FREECAD ASSEMBLY — COMPONENT RECIPES ("feeder_assembly")

This assembly document has 52 components, labeled P0..P51 below (a component is one placed body or linked part). 40 of them carry a construction recipe — the FreeCAD feature program that regenerates the part from scratch, quoted from this document or its linked companion documents; the rest are supplied as boundary geometry only. No exploded tour is included for this assembly.
NOTE — document 2 of 3 of this assembly tour. The two overview renders and the header above are repeated from document 1; the component sections below continue where the previous document stopped.
COMPONENT P15 — recipe-attached ("Body-slide_mid_v3", modeled in this document).
Construction recipe (the document's own serialized feature program — sketch geometry with constraints, then the solid features built on it; lengths are millimeters unless a unit is written):

FEATURE [Sketcher::SketchObject] Sketch077
  FullyConstrained = true
  MapMode = 5
  Support = -> [XY_Plane016]
  sketch-geometry (6):
    g0: LineSegment StartX=-11 StartY=0 StartZ=0 EndX=11 EndY=0 EndZ=0
    g1: LineSegment StartX=11 StartY=0 StartZ=0 EndX=11 EndY=-214 EndZ=0
    g2: LineSegment StartX=11 StartY=-214 StartZ=0 EndX=-11 EndY=-214 EndZ=0
    g3: LineSegment StartX=-11 StartY=-214 StartZ=0 EndX=-11 EndY=0 EndZ=0
    g4: LineSegment StartX=-11 StartY=0 StartZ=0 EndX=0 EndY=0 EndZ=0
    g5: LineSegment StartX=0 StartY=0 StartZ=0 EndX=11 EndY=0 EndZ=0
  constraints (16):
    c: Coincident(g0,g1)
    c: Coincident(g1,g2)
    c: Coincident(g2,g3)
    c: Horizontal(g0)
    c: Horizontal(g2)
    c: Vertical(g1)
    c: Vertical(g3)
    c: DistanceX(g0,g0) = 22
    c: DistanceY(g3,g3) = 214
    c: Coincident(g0,g3)
    c: PointOnObject(g-1,g0)
    c: Coincident(g4,g0)
    c: Coincident(g4,g-1)
    c: Coincident(g5,g4)
    c: Coincident(g5,g0)
    c: Equal(g4,g5)
FEATURE [PartDesign::Pad] Pad030  label="Pad-base_plate"
  Direction = (0,0,1)
  Length = 8
  Length2 = 10
  Profile = -> Sketch077
  ReferenceAxis = -> Sketch077 [N_Axis]
  Type = 0
FEATURE [Sketcher::SketchObject] Sketch078
  FullyConstrained = true
  MapMode = 5
  Placement = pos=(-11,0,0) rot=(0.57735,-0.57735,-0.57735;2.0944rad)
  Support = -> [Pad030]
FEATURE [Sketcher::SketchObject] Sketch079
  ExternalGeometry = -> [Pad030]
  FullyConstrained = true
  MapMode = 5
  Placement = pos=(0,0,8) rot=(0,0,1;0rad)
  Support = -> [Pad030]
  sketch-geometry (4):
    g0: LineSegment StartX=-11 StartY=2.5 StartZ=0 EndX=11 EndY=2.5 EndZ=0
    g1: LineSegment StartX=11 StartY=2.5 StartZ=0 EndX=11 EndY=-22.5 EndZ=0
    g2: LineSegment StartX=11 StartY=-22.5 StartZ=0 EndX=-11 EndY=-22.5 EndZ=0
    g3: LineSegment StartX=-11 StartY=-22.5 StartZ=0 EndX=-11 EndY=2.5 EndZ=0
  constraints (12):
    c: Coincident(g0,g1)
    c: Coincident(g1,g2)
    c: Coincident(g2,g3)
    c: Horizontal(g0)
    c: Horizontal(g2)
    c: Vertical(g1)
    c: Vertical(g3)
    c: DistanceY(g1,g1) = 25
    c: Coincident(g3,g0)
    c: PointOnObject(g1,g-3)
    c: Vertical(g0,g-4)
    c: DistanceY(g-4,g0) = 2.5
FEATURE [PartDesign::Pad] Pad031  label="Pad-bearing_mount_base"
  BaseFeature = -> Pad030
  Direction = (0,0,1)
  Length = 20
  Length2 = 8
  Profile = -> Sketch079
  ReferenceAxis = -> Sketch079 [N_Axis]
  Type = 4
FEATURE [Sketcher::SketchObject] Sketch080
  FullyConstrained = true
  MapMode = 5
  Placement = pos=(-11,0,0) rot=(0.57735,-0.57735,-0.57735;2.0944rad)
  Support = -> [Pad031]
  sketch-geometry (1):
    g0: Circle CenterX=10 CenterY=15 CenterZ=0 NormalX=0 NormalY=0 NormalZ=1 AngleXU=0 Radius=11.01
  constraints (3):
    c: DistanceX(g0) = 10
    c: DistanceY(g0) = 15
    c: Diameter(g0) = 22.02
FEATURE [PartDesign::Pocket] Pocket039  label="Pocket-bearing-OD"
  BaseFeature = -> Pad031
  Direction = (1,0,0)
  Length = 7
  Length2 = 5
  Profile = -> Sketch080
  ReferenceAxis = -> Sketch080 [N_Axis]
  Type = 0
FEATURE [PartDesign::Mirrored] Mirrored001  label="Mirrored-bearing_pocket"
  BaseFeature = -> Pocket039
  MirrorPlane = -> YZ_Plane016
  Originals = -> [Pocket039]
FEATURE [Sketcher::SketchObject] Sketch081
  ExternalGeometry = -> [Mirrored001]
  FullyConstrained = true
  MapMode = 5
  Placement = pos=(-4,0,0) rot=(0.57735,-0.57735,-0.57735;2.0944rad)
  Support = -> [Mirrored001]
  sketch-geometry (1):
    g0: Circle CenterX=10 CenterY=15 CenterZ=0 NormalX=0 NormalY=0 NormalZ=1 AngleXU=0 Radius=10
  constraints (2):
    c: Coincident(g0,g-3)
    c: Diameter(g0) = 20
FEATURE [PartDesign::Pocket] Pocket040
  BaseFeature = -> Mirrored001
  Direction = (1,0,0)
  Length = 5
  Length2 = 5
  Profile = -> Sketch081
  ReferenceAxis = -> Sketch081 [N_Axis]
  Type = 1
FEATURE [Sketcher::SketchObject] Sketch083
  ExternalGeometry = -> [Pocket040]
  FullyConstrained = false
  MapMode = 5
  Placement = pos=(-11,0,0) rot=(0.57735,-0.57735,-0.57735;2.0944rad)
  Support = -> [Pocket040]
  sketch-geometry (31):
    g0: LineSegment StartX=17.5 StartY=28 StartZ=0 EndX=17.5 EndY=93.7475 EndZ=0
    g1: LineSegment StartX=17.5 StartY=93.7475 StartZ=0 EndX=202.5 EndY=26.413 EndZ=0
    g2: LineSegment StartX=202.5 StartY=26.413 StartZ=0 EndX=202.5 EndY=8 EndZ=0
    g3: LineSegment StartX=165.375 StartY=8 StartZ=0 EndX=112 EndY=27.427 EndZ=0
    g4: LineSegment StartX=25 StartY=59.0924 StartZ=0 EndX=25 EndY=8 EndZ=0
    g5: LineSegment StartX=25 StartY=8 StartZ=0 EndX=22.5 EndY=8 EndZ=0
    g6: LineSegment StartX=22.5 StartY=8 StartZ=0 EndX=22.5 EndY=28 EndZ=0
    g7: LineSegment StartX=22.5 StartY=28 StartZ=0 EndX=17.5 EndY=28 EndZ=0
    g8: ArcOfCircle CenterX=30.2523 CenterY=73.1434 CenterZ=0 NormalX=0 NormalY=0 NormalZ=1 AngleXU=0 Radius=8 StartAngle=1.22173 EndAngle=4.36332
    g9: LineSegment StartX=27.5161 StartY=65.6259 StartZ=0 EndX=187.264 EndY=7.48246 EndZ=0
    g10: LineSegment StartX=192.736 StartY=22.5175 StartZ=0 EndX=32.9884 EndY=80.661 EndZ=0
    g11: LineSegment StartX=30.2523 StartY=73.1434 StartZ=0 EndX=190 EndY=15 EndZ=0
    g12: LineSegment StartX=77.1149 StartY=56.0868 StartZ=0 EndX=71.9846 EndY=41.9914 EndZ=0
    g13: LineSegment StartX=82.2452 StartY=70.1822 StartZ=0 EndX=77.1149 EndY=56.0868 EndZ=0
    g14: LineSegment StartX=102 StartY=31.0667 StartZ=0 EndX=102 EndY=8 EndZ=0
    g15: LineSegment StartX=102 StartY=8 StartZ=0 EndX=112 EndY=8 EndZ=0
    g16: LineSegment StartX=112 StartY=8 StartZ=0 EndX=112 EndY=27.427 EndZ=0
    g17: LineSegment StartX=102 StartY=31.0667 StartZ=0 EndX=25 EndY=59.0924 EndZ=0
    g18: GeomPoint X=72.1528 Y=42.4533 Z=0
    g19: LineSegment StartX=102 StartY=38.516 StartZ=0 EndX=102 EndY=55.5428 EndZ=0
    g20: LineSegment StartX=112 StartY=51.9031 StartZ=0 EndX=112 EndY=34.8763 EndZ=0
    g21: LineSegment StartX=32.9884 StartY=80.661 StartZ=0 EndX=102 EndY=55.5428 EndZ=0
    g22: LineSegment StartX=102 StartY=38.516 StartZ=0 EndX=27.5161 EndY=65.6259 EndZ=0
    g23: LineSegment StartX=112 StartY=51.9031 StartZ=0 EndX=192.736 EndY=22.5175 EndZ=0
    g24: LineSegment StartX=185.842 StartY=8 StartZ=0 EndX=165.375 EndY=8 EndZ=0
    g25: LineSegment StartX=202.5 StartY=8 StartZ=0 EndX=193.873 EndY=8 EndZ=0
    g26: LineSegment StartX=193.873 StartY=8 StartZ=0 EndX=185.842 EndY=8 EndZ=0
    g27: LineSegment StartX=187.264 StartY=7.48246 StartZ=0 EndX=185.842 EndY=8 EndZ=0
    g28: LineSegment StartX=185.842 StartY=8 StartZ=0 EndX=112 EndY=34.8763 EndZ=0
    g29: ArcOfCircle CenterX=190 CenterY=15 CenterZ=0 NormalX=0 NormalY=0 NormalZ=1 AngleXU=0 Radius=8 StartAngle=4.36332 EndAngle=5.21775
    g30: ArcOfCircle CenterX=190 CenterY=15 CenterZ=0 NormalX=0 NormalY=0 NormalZ=1 AngleXU=0 Radius=8 StartAngle=5.21775 EndAngle=7.50492
  constraints (84):
    c: PointOnObject(g0,g-5)
    c: Vertical(g0)
    c: Coincident(g1,g0)
    c: Coincident(g2,g1)
    c: PointOnObject(g2,g-3)
    c: Vertical(g2)
    c: PointOnObject(g25,g2)
    c: PointOnObject(g24,g-3)
    c: Coincident(g3,g24)
    c: Coincident(g4,g17)
    c: PointOnObject(g4,g-3)
    c: Vertical(g4)
    c: Coincident(g5,g4)
    c: Coincident(g5,g-4)
    c: Coincident(g6,g5)
    c: Coincident(g6,g-5)
    c: Coincident(g7,g6)
    c: Coincident(g7,g0)
    c: Parallel(g3,g1)
    c: Tangent(g8,g9) = -1.5708
    c: Tangent(g9,g29) = -1.5708
    c: Tangent(g30,g10) = -1.5708
    c: Tangent(g10,g8) = -1.5708
    c: Diameter(g8) = 16
    c: Coincident(g11,g8)
    c: Coincident(g11,g29)
    c: Parallel(g11,g3)
    c: Angle(g3,g-3) = 0.349066
    c: PointOnObject(g12,g11)
    c: PointOnObject(g12,g3)
    c: Angle(g3,g12) = 1.5708
    c: PointOnObject(g13,g1)
    c: Coincident(g13,g12)
    c: Parallel(g13,g12)
    c: Distance(g12,g17) = 50
    c: Distance(g13) = 15
    c: Distance(g12) = 15
    c: Distance(g10) = 170
    c: DistanceY(g2,g29) = 7
    c: DistanceX(g-5,g0) = 20
    c: DistanceX(g0,g4) = 7.5
    c: DistanceX(g4,g2) = 177.5
    c: DistanceX(g29,g2) = 12.5
    c: PointOnObject(g14,g-3)
    c: Coincident(g15,g14)
    c: PointOnObject(g15,g-3)
    c: Coincident(g16,g15)
    c: Vertical(g16)
    c: Vertical(g14)
    c: DistanceX(g15,g15) = 10
    c: DistanceX(g0,g14) = 84.5
    c: Coincident(g3,g16)
    c: Coincident(g17,g14)
    c: Parallel(g17,g3)
    c: PointOnObject(g18,g12)
    c: PointOnObject(g12,g17)
    c: PointOnObject(g19,g9)
    c: PointOnObject(g19,g10)
    c: PointOnObject(g20,g10)
    c: PointOnObject(g20,g9)
    c: Vertical(g20)
    c: Vertical(g14,g19)
    c: Vertical(g20,g3)
    c: Vertical(g19)
    c: Coincident(g21,g8)
    c: Coincident(g21,g19)
    c: Coincident(g22,g19)
    c: Coincident(g22,g8)
    c: Coincident(g23,g20)
    c: Coincident(g23,g30)
    c: Coincident(g27,g29)
    c: Coincident(g20,g28)
    c: Coincident(g26,g24)
    c: Horizontal(g24)
    c: Coincident(g25,g26)
    c: Horizontal(g25)
    c: Horizontal(g26)
    c: Coincident(g27,g28)
    c: Coincident(g27,g24)
    c: PointOnObject(g24,g9)
    c: Coincident(g29,g30)
    c: Coincident(g29,g30)
    c: Equal(g8,g29)
    c: Coincident(g25,g29)
FEATURE [PartDesign::Pad] Pad033  label="Pad-ramp001"
  BaseFeature = -> Pocket040
  Direction = (-1,0,0)
  Length = 22
  Length2 = 10
  Profile = -> Sketch083
  ReferenceAxis = -> Sketch083 [N_Axis]
  Reversed = true
  Type = 0
FEATURE [Sketcher::SketchObject] Sketch085
  ExternalGeometry = -> [Pad033]
  FullyConstrained = true
  MapMode = 5
  Placement = pos=(-11,0,0) rot=(0.57735,-0.57735,-0.57735;2.0944rad)
  Support = -> [Pad033]
  sketch-geometry (6):
    g0: ArcOfCircle CenterX=30.2523 CenterY=73.1434 CenterZ=0 NormalX=0 NormalY=0 NormalZ=1 AngleXU=0 Radius=11.25 StartAngle=1.22173 EndAngle=4.36332
    g1: ArcOfCircle CenterX=190 CenterY=15 CenterZ=0 NormalX=0 NormalY=0 NormalZ=1 AngleXU=0 Radius=11.25 StartAngle=4.36332 EndAngle=7.50492
    g2: LineSegment StartX=26.4045 StartY=62.5719 StartZ=0 EndX=186.152 EndY=4.42846 EndZ=0
    g3: LineSegment StartX=193.848 StartY=25.5715 StartZ=0 EndX=34.1 EndY=83.715 EndZ=0
    g4: LineSegment StartX=30.2523 StartY=73.1434 StartZ=0 EndX=190 EndY=15 EndZ=0
    g5: LineSegment StartX=55.3826 StartY=79.9594 StartZ=0 EndX=50.2523 EndY=65.864 EndZ=0
  constraints (17):
    c: Tangent(g0,g2) = -1.5708
    c: Tangent(g2,g1) = -1.5708
    c: Tangent(g3,g0) = -1.5708
    c: Equal(g0,g1)
    c: Diameter(g0) = 22.5
    c: Coincident(g4,g0)
    c: Coincident(g4,g1)
    c: Distance(g3) = 170
    c: DistanceX(g1,g-3) = 12.5
    c: PointOnObject(g5,g-4)
    c: PointOnObject(g5,g4)
    c: Angle(g4,g5) = 1.5708
    c: Distance(g5) = 15
    c: Parallel(g-4,g4)
    c: Angle(g1) = 3.14159
    c: Coincident(g3,g1)
    c: DistanceX(g0,g5) = 20
FEATURE [PartDesign::Pocket] Pocket043  label="Pocket-bearing_slot001"
  BaseFeature = -> Pad033
  Direction = (1,0,0)
  Length = 7.5
  Length2 = 5
  Profile = -> Sketch085
  ReferenceAxis = -> Sketch085 [N_Axis]
  Type = 0
FEATURE [PartDesign::Mirrored] Mirrored003  label="Mirrored-bearing_slot"
  BaseFeature = -> Pocket043
  MirrorPlane = -> YZ_Plane016
  Originals = -> [Pocket043]
FEATURE [Sketcher::SketchObject] Sketch094
  ExternalGeometry = -> [Mirrored003]
  FullyConstrained = true
  MapMode = 5
  Placement = pos=(-3.5,0,0) rot=(0.57735,-0.57735,-0.57735;2.0944rad)
  Support = -> [Mirrored003]
  sketch-geometry (4):
    g0: LineSegment StartX=112 StartY=34.8763 StartZ=0 EndX=102 EndY=38.516 EndZ=0
    g1: LineSegment StartX=102 StartY=38.516 StartZ=0 EndX=102 EndY=55.5428 EndZ=0
    g2: LineSegment StartX=102 StartY=55.5428 StartZ=0 EndX=112 EndY=51.9031 EndZ=0
    g3: LineSegment StartX=112 StartY=51.9031 StartZ=0 EndX=112 EndY=34.8763 EndZ=0
  constraints (8):
    c: Coincident(g1,g0)
    c: Coincident(g2,g1)
    c: Coincident(g3,g2)
    c: Coincident(g3,g0)
    c: Coincident(g1,g-4)
    c: Coincident(g0,g-4)
    c: Coincident(g-3,g2)
    c: Coincident(g-3,g0)
FEATURE [PartDesign::Pocket] Pocket044  label="Pocket-mid_support_inside"
  BaseFeature = -> Mirrored003
  Direction = (1,0,0)
  Length = 2.5
  Length2 = 5
  Profile = -> Sketch094
  ReferenceAxis = -> Sketch094 [N_Axis]
  Type = 0
FEATURE [PartDesign::Mirrored] Mirrored004
  BaseFeature = -> Pocket044
  MirrorPlane = -> YZ_Plane016
  Originals = -> [Pocket044]
FEATURE [Sketcher::SketchObject] Sketch095
  ExternalGeometry = -> [Mirrored004,Sketch085]
  FullyConstrained = true
  MapMode = 5
  Placement = pos=(-11,0,0) rot=(0.57735,-0.57735,-0.57735;2.0944rad)
  Support = -> [Mirrored004]
  sketch-geometry (9):
    g0: LineSegment StartX=17.5 StartY=93.7475 StartZ=0 EndX=202.5 EndY=26.413 EndZ=0
    g1: LineSegment StartX=202.5 StartY=26.413 StartZ=0 EndX=202.5 EndY=0 EndZ=0
    g2: LineSegment StartX=202.5 StartY=0 StartZ=0 EndX=187.355 EndY=0 EndZ=0
    g3: LineSegment StartX=187.355 StartY=0 StartZ=0 EndX=17.5 EndY=61.8222 EndZ=0
    g4: LineSegment StartX=17.5 StartY=61.8222 StartZ=0 EndX=17.5 EndY=93.7475 EndZ=0
    g5: ArcOfCircle CenterX=30.2523 CenterY=73.1434 CenterZ=0 NormalX=0 NormalY=0 NormalZ=1 AngleXU=0 Radius=6 StartAngle=1.22173 EndAngle=4.36332
    g6: ArcOfCircle CenterX=190 CenterY=15 CenterZ=0 NormalX=0 NormalY=0 NormalZ=1 AngleXU=0 Radius=6 StartAngle=4.36332 EndAngle=7.50492
    g7: LineSegment StartX=28.2001 StartY=67.5053 StartZ=0 EndX=187.948 EndY=9.36184 EndZ=0
    g8: LineSegment StartX=192.052 StartY=20.6382 StartZ=0 EndX=32.3044 EndY=78.7816 EndZ=0
  constraints (21):
    c: Coincident(g0,g-4)
    c: Coincident(g0,g-6)
    c: Coincident(g1,g0)
    c: PointOnObject(g1,g-7)
    c: Vertical(g1)
    c: Coincident(g2,g1)
    c: PointOnObject(g2,g-7)
    c: Coincident(g3,g2)
    c: PointOnObject(g3,g-4)
    c: Coincident(g4,g3)
    c: Coincident(g4,g0)
    c: Parallel(g-5,g3)
    c: PointOnObject(g-5,g3)
    c: Tangent(g5,g7) = -1.5708
    c: Tangent(g7,g6) = -1.5708
    c: Tangent(g6,g8) = -1.5708
    c: Tangent(g8,g5) = -1.5708
    c: Equal(g5,g6)
    c: Coincident(g5,g-9)
    c: Coincident(g6,g-8)
    c: Diameter(g6) = 12
FEATURE [PartDesign::Pad] Pad039  label="Pad-bearing_cap"
  BaseFeature = -> Mirrored004
  Direction = (-1,0,0)
  Length = 2.5
  Length2 = 10
  Profile = -> Sketch095
  ReferenceAxis = -> Sketch095 [N_Axis]
  Type = 0
FEATURE [PartDesign::Mirrored] Mirrored005
  BaseFeature = -> Pad039
  MirrorPlane = -> YZ_Plane016
  Originals = -> [Pad039]
FEATURE [PartDesign::Fillet] Fillet021
  Base = -> Mirrored005 [Edge81,Edge94,Edge122]
  BaseFeature = -> Mirrored005
  Radius = 14
  SupportTransform = false
  UseAllEdges = false
FEATURE [PartDesign::Fillet] Fillet022
  Base = -> Fillet021 [Edge45]
  BaseFeature = -> Fillet021
  Radius = 14
  SupportTransform = false
  UseAllEdges = false
FEATURE [PartDesign::Fillet] Fillet023  label="Fillet-bottom_face_to_vertical"
  Base = -> Fillet022 [Edge121,Edge122,Edge120]
  BaseFeature = -> Fillet022
  Radius = 2
  SupportTransform = false
  UseAllEdges = false
FEATURE [PartDesign::Fillet] Fillet024  label="Fillet-acute_end_angle"
  Base = -> Fillet023 [Edge32]
  BaseFeature = -> Fillet023
  Radius = 2
  SupportTransform = false
  UseAllEdges = false
FEATURE [PartDesign::Fillet] Fillet025
  Base = -> Fillet024 [Edge107]
  BaseFeature = -> Fillet024
  Radius = 5
  SupportTransform = false
  UseAllEdges = false
FEATURE [PartDesign::Fillet] Fillet026
  Base = -> Fillet025 [Edge62]
  BaseFeature = -> Fillet025
  Radius = 12
  SupportTransform = false
  UseAllEdges = false
FEATURE [PartDesign::Fillet] Fillet027
  Base = -> Fillet026 [Edge25]
  BaseFeature = -> Fillet026
  Radius = 2
  SupportTransform = false
  UseAllEdges = false
FEATURE [PartDesign::Fillet] Fillet028
  Base = -> Fillet027 [Edge231,Edge246]
  BaseFeature = -> Fillet027
  Radius = 3
  SupportTransform = false
  UseAllEdges = false
FEATURE [PartDesign::Fillet] Fillet029
  Base = -> Fillet028 [Edge51,Edge54]
  BaseFeature = -> Fillet028
  Radius = 3
  SupportTransform = false
  UseAllEdges = false
FEATURE [PartDesign::Fillet] Fillet030  label="Fillet-extender_main_curvature"
  Base = -> Fillet029 [Edge176,Edge209]
  BaseFeature = -> Fillet029
  Radius = 10
  SupportTransform = false
  UseAllEdges = false
FEATURE [PartDesign::Fillet] Fillet031  label="Fillet-bearing_face"
  Base = -> Fillet030 [Face16]
  BaseFeature = -> Fillet030
  Radius = 0.4
  SupportTransform = false
  UseAllEdges = false
FEATURE [PartDesign::Fillet] Fillet032  label="Fillet-bearing_face_mirror"
  Base = -> Fillet031 [Face28]
  BaseFeature = -> Fillet031
  Radius = 0.4
  SupportTransform = false
  UseAllEdges = false
FEATURE [PartDesign::Fillet] Fillet033
  Base = -> Fillet032 [Face96,Face112]
  BaseFeature = -> Fillet032
  Radius = 1
  SupportTransform = false
  UseAllEdges = false
FEATURE [PartDesign::Fillet] Fillet034
  Base = -> Fillet033 [Face119,Face4]
  BaseFeature = -> Fillet033
  Radius = 0.4
  SupportTransform = false
  UseAllEdges = false
FEATURE [Sketcher::SketchObject] Sketch098
  ExternalGeometry = -> [Fillet021]
  FullyConstrained = true
  MapMode = 5
  Placement = pos=(0,0,8) rot=(0,0,1;0rad)
  Support = -> [Fillet034]
  sketch-geometry (8):
    g0: ArcOfCircle CenterX=-2e-16 CenterY=-40 CenterZ=0 NormalX=0 NormalY=0 NormalZ=1 AngleXU=0 Radius=6 StartAngle=-1.8e-15 EndAngle=3.14159
    g1: ArcOfCircle CenterX=0 CenterY=-80 CenterZ=0 NormalX=0 NormalY=0 NormalZ=1 AngleXU=0 Radius=6 StartAngle=3.14159 EndAngle=6.28319
    g2: LineSegment StartX=-6 StartY=-40 StartZ=0 EndX=-6 EndY=-80 EndZ=0
    g3: LineSegment StartX=6 StartY=-80 StartZ=0 EndX=6 EndY=-40 EndZ=0
    g4: ArcOfCircle CenterX=0 CenterY=-120 CenterZ=0 NormalX=0 NormalY=0 NormalZ=1 AngleXU=0 Radius=6 StartAngle=4e-16 EndAngle=3.14159
    g5: ArcOfCircle CenterX=0 CenterY=-140 CenterZ=0 NormalX=0 NormalY=0 NormalZ=1 AngleXU=0 Radius=6 StartAngle=3.14159 EndAngle=6.28319
    g6: LineSegment StartX=-6 StartY=-120 StartZ=0 EndX=-6 EndY=-140 EndZ=0
    g7: LineSegment StartX=6 StartY=-140 StartZ=0 EndX=6 EndY=-120 EndZ=0
  constraints (20):
    c: Tangent(g0,g2) = -1.5708
    c: Tangent(g2,g1) = -1.5708
    c: Tangent(g1,g3) = -1.5708
    c: Tangent(g3,g0) = -1.5708
    c: Equal(g0,g1)
    c: DistanceX(g-3,g0) = 11
    c: Diameter(g1) = 12
    c: DistanceY(g0) = -40
    c: DistanceY(g2,g2) = 40
    c: Tangent(g4,g6) = -1.5708
    c: Tangent(g6,g5) = -1.5708
    c: Tangent(g5,g7) = -1.5708
    c: Tangent(g7,g4) = -1.5708
    c: Equal(g4,g5)
    c: PointOnObject(g4,g-2)
    c: PointOnObject(g5,g-2)
    c: DistanceY(g6,g6) = 20
    c: Diameter(g5) = 12
    c: DistanceY(g4,g1) = 40
    c: PointOnObject(g1,g-2)
FEATURE [PartDesign::Pocket] Pocket051
  BaseFeature = -> Fillet034
  Direction = (0,0,-1)
  Length = 5
  Length2 = 5
  Profile = -> Sketch098
  ReferenceAxis = -> Sketch098 [N_Axis]
  Type = 0
FEATURE [Sketcher::SketchObject] Sketch100
  FullyConstrained = false
  MapMode = 5
  Placement = pos=(0,0,8) rot=(0,0,1;0rad)
  Support = -> [Pocket051]
  sketch-geometry (1):
    g0: Circle CenterX=0 CenterY=-207 CenterZ=0 NormalX=0 NormalY=0 NormalZ=1 AngleXU=0 Radius=6
  constraints (2):
    c: PointOnObject(g0,g-2)
    c: Diameter(g0) = 12
FEATURE [PartDesign::Pocket] Pocket052  label="Pocket-extender_inset"
  BaseFeature = -> Pocket051
  Direction = (0,0,-1)
  Length = 5
  Length2 = 40
  Profile = -> Sketch100
  ReferenceAxis = -> Sketch100 [N_Axis]
  Type = 4
FEATURE [Sketcher::SketchObject] Sketch101
  FullyConstrained = false
  MapMode = 5
  Placement = pos=(-11,0,0) rot=(0.57735,-0.57735,-0.57735;2.0944rad)
  sketch-geometry (9):
    g0: LineSegment StartX=25 StartY=59.0924 StartZ=0 EndX=25 EndY=55.5221 EndZ=0
    g1: LineSegment StartX=25 StartY=59.0924 StartZ=0 EndX=28.3551 EndY=57.8713 EndZ=0
    g2: ArcOfCircle CenterX=27.5 CenterY=55.5221 CenterZ=0 NormalX=0 NormalY=0 NormalZ=1 AngleXU=0 Radius=2.5 StartAngle=1.22173 EndAngle=3.14159
    g3: ArcOfCircle CenterX=97 CenterY=27.5657 CenterZ=0 NormalX=0 NormalY=0 NormalZ=1 AngleXU=0 Radius=5 StartAngle=2.0166e-12 EndAngle=1.22173
    g4: ArcOfCircle CenterX=114.5 CenterY=23.8566 CenterZ=0 NormalX=0 NormalY=0 NormalZ=1 AngleXU=0 Radius=2.5 StartAngle=1.22173 EndAngle=3.14159
    g5: LineSegment StartX=98.7101 StartY=32.2641 StartZ=0 EndX=102 EndY=31.0667 EndZ=0
    g6: LineSegment StartX=102 StartY=31.0667 StartZ=0 EndX=102 EndY=27.5657 EndZ=0
    g7: LineSegment StartX=112 StartY=23.8566 StartZ=0 EndX=112 EndY=27.427 EndZ=0
    g8: LineSegment StartX=112 StartY=27.427 StartZ=0 EndX=115.355 EndY=26.2059 EndZ=0
  constraints (18):
    c: Coincident(g1,g0)
    c: Coincident(g0,g2)
    c: Coincident(g1,g2)
    c: Diameter(g2) = 5
    c: Coincident(g5,g3)
    c: Coincident(g6,g5)
    c: Coincident(g6,g3)
    c: Coincident(g7,g4)
    c: Coincident(g8,g7)
    c: Coincident(g8,g4)
    c: Diameter(g3) = 10
    c: Angle(g3) = 1.22173
    c: Equal(g6,g5)
    c: Equal(g8,g7)
    c: Angle(g4) = 1.91986
    c: Equal(g0,g1)
    c: Angle(g2) = 1.91986
    c: Equal(g4,g2)
FEATURE [PartDesign::Body] Body017  label="Body-slide_mid_v3"
  Group = -> [Sketch077,Pad030,Sketch078,Sketch079,Pad031,Sketch080,Pocket039,Mirrored001,Sketch081,Pocket040,Sketch083,Pad033,Sketch085,Pocket043,Mirrored003,Sketch094,Pocket044,Mirrored004,Sketch095,Pad039,Mirrored005,Fillet021,Sketch098,Sketch100,Fillet022,Fillet023,Fillet024,Fillet025,Fillet026,Fillet027,Fillet028,Fillet029,Fillet030,Fillet031,Fillet032,Fillet033,Fillet034,Pocket051,Pocket052,Sketch101,+13 more]
  Origin = -> Origin016
  Tip = -> Fillet125
COMPONENT P16 — recipe-attached ("Body-bearing001", modeled in this document).
Construction recipe (the document's own serialized feature program — sketch geometry with constraints, then the solid features built on it; lengths are millimeters unless a unit is written):

FEATURE [Sketcher::SketchObject] Sketch082
  FullyConstrained = true
  MapMode = 5
  Support = -> [XY_Plane017]
  sketch-geometry (2):
    g0: Circle CenterX=0 CenterY=0 CenterZ=0 NormalX=0 NormalY=0 NormalZ=1 AngleXU=0 Radius=3.95
    g1: Circle CenterX=0 CenterY=0 CenterZ=0 NormalX=0 NormalY=0 NormalZ=1 AngleXU=0 Radius=11
  constraints (4):
    c: Coincident(g0,g-1)
    c: Coincident(g1,g0)
    c: Diameter(g0) = 7.9
    c: Diameter(g1) = 22
FEATURE [PartDesign::Pad] Pad032
  Direction = (0,0,1)
  Length = 7
  Length2 = 10
  Profile = -> Sketch082
  ReferenceAxis = -> Sketch082 [N_Axis]
  Type = 0
FEATURE [PartDesign::Body] Body018  label="Body-bearing001"
  Group = -> [Sketch082,Pad032]
  Origin = -> Origin017
  Placement = pos=(-3.26003,-10.1498,15.02) rot=(0,-1,0;1.5708rad)
  Tip = -> Pad032
COMPONENT P17 — recipe-attached ("Body-v3.1_slicer", modeled in this document).
Construction recipe (the document's own serialized feature program — sketch geometry with constraints, then the solid features built on it; lengths are millimeters unless a unit is written):

FEATURE [Sketcher::SketchObject] Sketch086
  FullyConstrained = true
  MapMode = 5
  Placement = pos=(0,0,0) rot=(1,0,0;1.5708rad)
  Support = -> [XZ_Plane018]
  sketch-geometry (16):
    g0: LineSegment StartX=-3.8476e-12 StartY=-10.8333 StartZ=0 EndX=4 EndY=-10.8333 EndZ=0
    g1: LineSegment StartX=4 StartY=-10.8333 StartZ=0 EndX=4 EndY=-0.833334 EndZ=0
    g2: LineSegment StartX=4 StartY=-0.833334 StartZ=0 EndX=-15 EndY=-0.833334 EndZ=0
    g3: LineSegment StartX=-15 StartY=-0.833334 StartZ=0 EndX=-15 EndY=0.833334 EndZ=0
    g4: LineSegment StartX=-15 StartY=0.833334 StartZ=0 EndX=4 EndY=0.833334 EndZ=0
    g5: LineSegment StartX=4 StartY=0.833334 StartZ=0 EndX=4 EndY=10.8333 EndZ=0
    g6: LineSegment StartX=4 StartY=10.8333 StartZ=0 EndX=0 EndY=10.8333 EndZ=0
    g7: LineSegment StartX=0 StartY=10.8333 StartZ=0 EndX=0 EndY=0.853333 EndZ=0
    g8: LineSegment StartX=0 StartY=0.853333 StartZ=0 EndX=-19 EndY=0.853333 EndZ=0
    g9: LineSegment StartX=-19 StartY=0.853333 StartZ=0 EndX=-19 EndY=-0.853333 EndZ=0
    g10: LineSegment StartX=-19 StartY=-0.853333 StartZ=0 EndX=-3.8476e-12 EndY=-0.853333 EndZ=0
    g11: LineSegment StartX=-3.8476e-12 StartY=-0.853333 StartZ=0 EndX=-3.8476e-12 EndY=-10.8333 EndZ=0
    g12: LineSegment StartX=-19 StartY=0.853333 StartZ=0 EndX=-15 EndY=-0.833334 EndZ=0
    g13: LineSegment StartX=-15 StartY=0.833334 StartZ=0 EndX=-19 EndY=-0.853333 EndZ=0
    g14: LineSegment StartX=0 StartY=0.853333 StartZ=0 EndX=0 EndY=0 EndZ=0
    g15: LineSegment StartX=0 StartY=0 StartZ=0 EndX=-3.8476e-12 EndY=-0.853333 EndZ=0
  constraints (44):
    c: Horizontal(g0)
    c: Coincident(g1,g0)
    c: Vertical(g1)
    c: Coincident(g2,g1)
    c: Horizontal(g2)
    c: Coincident(g3,g2)
    c: Vertical(g3)
    c: Horizontal(g4)
    c: Coincident(g5,g4)
    c: Vertical(g5)
    c: Coincident(g6,g5)
    c: PointOnObject(g6,g-2)
    c: Horizontal(g6)
    c: Coincident(g7,g6)
    c: Vertical(g7)
    c: Coincident(g8,g7)
    c: Horizontal(g8)
    c: Coincident(g9,g8)
    c: Vertical(g9)
    c: Coincident(g10,g9)
    c: Horizontal(g10)
    c: Coincident(g11,g10)
    c: Vertical(g11)
    c: DistanceY(g3,g3) = 1.66667
    c: Coincident(g3,g4)
    c: DistanceY(g9,g9) = 1.70667
    c: Coincident(g12,g8)
    c: Coincident(g12,g2)
    c: Coincident(g13,g3)
    c: Coincident(g13,g9)
    c: Equal(g13,g12)
    c: DistanceX(g9,g2) = 4
    c: DistanceX(g0,g0) = 4
    c: Equal(g0,g6)
    c: Equal(g1,g5)
    c: DistanceY(g1,g1) = 10
    c: DistanceX(g2,g10) = 15
    c: Coincident(g11,g0)
    c: Vertical(g1,g4)
    c: Coincident(g14,g7)
    c: Coincident(g14,g-1)
    c: Coincident(g15,g14)
    c: Coincident(g15,g10)
    c: Equal(g15,g14)
FEATURE [PartDesign::Pad] Pad034  label="Pad-main_body001"
  Direction = (0,-1,-2e-16)
  Length = 93
  Length2 = 10
  Placement = pos=(0,0,0) rot=(1,0,0;1.5708rad)
  Profile = -> Sketch086
  ReferenceAxis = -> Sketch086 [N_Axis]
  Type = 0
FEATURE [Sketcher::SketchObject] Sketch087
  ExternalGeometry = -> [Pad034]
  FullyConstrained = true
  MapMode = 5
  Placement = pos=(0,2e-16,0.853333) rot=(0,0,1;3.14159rad)
  Support = -> [Pad034]
  sketch-geometry (14):
    g0: ArcOfCircle CenterX=5.5 CenterY=23 CenterZ=0 NormalX=0 NormalY=0 NormalZ=1 AngleXU=0 Radius=1.7 StartAngle=1.5708 EndAngle=4.71239
    g1: ArcOfCircle CenterX=11.5 CenterY=23 CenterZ=0 NormalX=0 NormalY=0 NormalZ=1 AngleXU=0 Radius=1.7 StartAngle=4.71239 EndAngle=7.85398
    g2: LineSegment StartX=5.5 StartY=21.3 StartZ=0 EndX=11.5 EndY=21.3 EndZ=0
    g3: LineSegment StartX=11.5 StartY=24.7 StartZ=0 EndX=5.5 EndY=24.7 EndZ=0
    g4: ArcOfCircle CenterX=5.5 CenterY=48 CenterZ=0 NormalX=0 NormalY=0 NormalZ=1 AngleXU=0 Radius=1.7 StartAngle=1.5708 EndAngle=4.71239
    g5: ArcOfCircle CenterX=11.5 CenterY=48 CenterZ=0 NormalX=0 NormalY=0 NormalZ=1 AngleXU=0 Radius=1.7 StartAngle=4.71239 EndAngle=7.85398
    g6: LineSegment StartX=5.5 StartY=46.3 StartZ=0 EndX=11.5 EndY=46.3 EndZ=0
    g7: LineSegment StartX=11.5 StartY=49.7 StartZ=0 EndX=5.5 EndY=49.7 EndZ=0
    g8: ArcOfCircle CenterX=5.5 CenterY=73 CenterZ=0 NormalX=0 NormalY=0 NormalZ=1 AngleXU=0 Radius=1.7 StartAngle=1.5708 EndAngle=4.71239
    g9: ArcOfCircle CenterX=11.5 CenterY=73 CenterZ=0 NormalX=0 NormalY=0 NormalZ=1 AngleXU=0 Radius=1.7 StartAngle=4.71239 EndAngle=7.85398
    g10: LineSegment StartX=5.5 StartY=71.3 StartZ=0 EndX=11.5 EndY=71.3 EndZ=0
    g11: LineSegment StartX=11.5 StartY=74.7 StartZ=0 EndX=5.5 EndY=74.7 EndZ=0
    g12: LineSegment StartX=11.5 StartY=73 StartZ=0 EndX=11.5 EndY=48 EndZ=0
    g13: LineSegment StartX=11.5 StartY=48 StartZ=0 EndX=11.5 EndY=23 EndZ=0
  constraints (34):
    c: Tangent(g0,g2) = -1.5708
    c: Tangent(g2,g1) = -1.5708
    c: Tangent(g1,g3) = -1.5708
    c: Tangent(g3,g0) = -1.5708
    c: Equal(g0,g1)
    c: Horizontal(g2)
    c: Diameter(g1) = 3.4
    c: DistanceX(g2,g2) = 6
    c: DistanceX(g1,g-3) = 7.5
    c: Tangent(g4,g6) = -1.5708
    c: Tangent(g6,g5) = -1.5708
    c: Tangent(g5,g7) = -1.5708
    c: Tangent(g7,g4) = -1.5708
    c: Equal(g4,g5)
    c: Tangent(g8,g10) = -1.5708
    c: Tangent(g10,g9) = -1.5708
    c: Tangent(g9,g11) = -1.5708
    c: Tangent(g11,g8) = -1.5708
    c: Equal(g8,g9)
    c: Equal(g9,g5)
    c: Equal(g5,g1)
    c: Horizontal(g5,g4)
    c: Horizontal(g9,g8)
    c: Vertical(g8,g4)
    c: Vertical(g4,g0)
    c: Coincident(g12,g9)
    c: Coincident(g12,g5)
    c: Vertical(g12)
    c: Coincident(g13,g5)
    c: Coincident(g13,g1)
    c: Vertical(g13)
    c: Equal(g12,g13)
    c: DistanceY(g12,g12) = 25
    c: DistanceY(g9,g-3) = 20
FEATURE [PartDesign::Pad] Pad035  label="Pad-slots001"
  BaseFeature = -> Pad034
  Direction = (0,-2e-16,1)
  Length = 10
  Length2 = 10
  Placement = pos=(0,0,0) rot=(1,0,0;1.5708rad)
  Profile = -> Sketch087
  ReferenceAxis = -> Sketch087 [N_Axis]
  Type = 0
FEATURE [PartDesign::Mirrored] Mirrored002  label="Mirrored-slots_top_to_bottom001"
  BaseFeature = -> Pad035
  MirrorPlane = -> XY_Plane018
  Originals = -> [Pad035]
  Placement = pos=(0,0,0) rot=(1,0,0;1.5708rad)
FEATURE [Sketcher::SketchObject] Sketch088
  ExternalGeometry = -> [Mirrored002]
  FullyConstrained = true
  MapMode = 5
  Placement = pos=(0,-2e-16,-0.833334) rot=(0,0,1;3.14159rad)
  Support = -> [Mirrored002]
  sketch-geometry (5):
    g0: Circle CenterX=7.5 CenterY=23 CenterZ=0 NormalX=0 NormalY=0 NormalZ=1 AngleXU=0 Radius=1.69
    g1: Circle CenterX=7.5 CenterY=48 CenterZ=0 NormalX=0 NormalY=0 NormalZ=1 AngleXU=0 Radius=1.69
    g2: Circle CenterX=7.5 CenterY=73 CenterZ=0 NormalX=0 NormalY=0 NormalZ=1 AngleXU=0 Radius=1.69
    g3: LineSegment StartX=7.5 StartY=73 StartZ=0 EndX=7.5 EndY=48 EndZ=0
    g4: LineSegment StartX=7.5 StartY=48 StartZ=0 EndX=7.5 EndY=23 EndZ=0
  constraints (13):
    c: Equal(g2,g1)
    c: Equal(g2,g0)
    c: Diameter(g2) = 3.38
    c: Coincident(g3,g2)
    c: Coincident(g3,g1)
    c: Vertical(g3)
    c: Coincident(g4,g1)
    c: Coincident(g4,g0)
    c: Vertical(g4)
    c: DistanceY(g3,g3) = 25
    c: DistanceX(g0,g-3) = 7.5
    c: Equal(g3,g4)
    c: DistanceY(g2,g-3) = 20
FEATURE [PartDesign::Pad] Pad036  label="Pad-inside_holes001"
  BaseFeature = -> Mirrored002
  Direction = (0,-2e-16,1)
  Length = 10
  Length2 = 10
  Placement = pos=(0,0,0) rot=(1,0,0;1.5708rad)
  Profile = -> Sketch088
  ReferenceAxis = -> Sketch088 [N_Axis]
  Type = 0
FEATURE [Sketcher::SketchObject] Sketch089
  FullyConstrained = true
  MapMode = 5
  Placement = pos=(0,0,0) rot=(0.707107,0,-0.707107;3.14159rad)
  Support = -> [Pad036]
  sketch-geometry (1):
    g0: Circle CenterX=0 CenterY=3 CenterZ=0 NormalX=0 NormalY=0 NormalZ=1 AngleXU=0 Radius=4.55
  constraints (3):
    c: PointOnObject(g0,g-2)
    c: Diameter(g0) = 9.1
    c: DistanceY(g-1,g0) = 3
FEATURE [PartDesign::Pad] Pad037  label="Pad-shaft_female"
  BaseFeature = -> Pad036
  Direction = (-1,0,-2e-16)
  Length = 19
  Length2 = 10
  Placement = pos=(0,0,0) rot=(1,0,0;1.5708rad)
  Profile = -> Sketch089
  ReferenceAxis = -> Sketch089 [N_Axis]
  Type = 0
FEATURE [Sketcher::SketchObject] Sketch092
  ExternalGeometry = -> [Pad037]
  FullyConstrained = true
  MapMode = 5
  Placement = pos=(0,0,0) rot=(-1,0,0;1.5708rad)
  Support = -> [Pad037]
  sketch-geometry (4):
    g0: LineSegment StartX=-3.8476e-12 StartY=10.8333 StartZ=0 EndX=4 EndY=10.8333 EndZ=0
    g1: LineSegment StartX=4 StartY=10.8333 StartZ=0 EndX=4 EndY=-10.8333 EndZ=0
    g2: LineSegment StartX=4 StartY=-10.8333 StartZ=0 EndX=-3.8476e-12 EndY=-10.8333 EndZ=0
    g3: LineSegment StartX=-3.8476e-12 StartY=-10.8333 StartZ=0 EndX=-3.8476e-12 EndY=10.8333 EndZ=0
  constraints (10):
    c: Coincident(g0,g1)
    c: Coincident(g1,g2)
    c: Coincident(g2,g3)
    c: Coincident(g3,g0)
    c: Horizontal(g0)
    c: Horizontal(g2)
    c: Vertical(g1)
    c: Vertical(g3)
    c: Coincident(g0,g-3)
    c: Coincident(g1,g-4)
FEATURE [PartDesign::Pad] Pad038  label="Pad-gap_extension"
  BaseFeature = -> Pad037
  Direction = (0,1,2e-16)
  Length = 10
  Length2 = 10
  Placement = pos=(0,0,0) rot=(1,0,0;1.5708rad)
  Profile = -> Sketch092
  ReferenceAxis = -> Sketch092 [N_Axis]
  Type = 0
FEATURE [Sketcher::SketchObject] Sketch093
  ExternalGeometry = -> [Pad038]
  FullyConstrained = true
  MapMode = 5
  Placement = pos=(4,0,0) rot=(0.707107,0,0.707107;3.14159rad)
  Support = -> [Pad038]
  sketch-geometry (6):
    g0: ArcOfCircle CenterX=0 CenterY=3 CenterZ=0 NormalX=0 NormalY=0 NormalZ=1 AngleXU=0 Radius=4.5 StartAngle=1.75706 EndAngle=7.66772
    g1: GeomPoint X=-0.833334 Y=7.42217 Z=0
    g2: GeomPoint X=0.833334 Y=7.42217 Z=0
    g3: LineSegment StartX=-0.833334 StartY=7.42217 StartZ=0 EndX=-0.833334 EndY=8.42217 EndZ=0
    g4: LineSegment StartX=-0.833334 StartY=8.42217 StartZ=0 EndX=0.833334 EndY=8.42217 EndZ=0
    g5: LineSegment StartX=0.833334 StartY=8.42217 StartZ=0 EndX=0.833334 EndY=7.42217 EndZ=0
  constraints (15):
    c: PointOnObject(g0,g-2)
    c: DistanceY(g0) = 3
    c: Diameter(g0) = 9
    c: PointOnObject(g1,g-3)
    c: PointOnObject(g2,g-4)
    c: Coincident(g3,g1)
    c: PointOnObject(g3,g-3)
    c: Coincident(g4,g3)
    c: PointOnObject(g4,g-4)
    c: Horizontal(g4)
    c: Coincident(g5,g4)
    c: Coincident(g5,g2)
    c: Coincident(g0,g5)
    c: Coincident(g0,g3)
    c: DistanceY(g5,g5) = 1
FEATURE [PartDesign::Pocket] Pocket042  label="Pocket-shaft_male"
  BaseFeature = -> Pad038
  Direction = (-1,0,2e-16)
  Length = 19
  Length2 = 5
  Placement = pos=(0,0,0) rot=(1,0,0;1.5708rad)
  Profile = -> Sketch093
  ReferenceAxis = -> Sketch093 [N_Axis]
  Type = 0
FEATURE [PartDesign::Fillet] Fillet014
  Base = -> Pocket042 [Edge69,Edge125,Edge59,Edge64,Edge62]
  BaseFeature = -> Pocket042
  Placement = pos=(0,0,0) rot=(1,0,0;1.5708rad)
  Radius = 0.45
  SupportTransform = false
  UseAllEdges = false
FEATURE [PartDesign::Fillet] Fillet015
  Base = -> Fillet014 [Edge64,Edge42]
  BaseFeature = -> Fillet014
  Placement = pos=(0,0,0) rot=(1,0,0;1.5708rad)
  Radius = 1
  SupportTransform = false
  UseAllEdges = false
FEATURE [PartDesign::Fillet] Fillet016
  Base = -> Fillet015 [Edge140,Edge141,Edge138,Edge132]
  BaseFeature = -> Fillet015
  Placement = pos=(0,0,0) rot=(1,0,0;1.5708rad)
  Radius = 1
  SupportTransform = false
  UseAllEdges = false
FEATURE [PartDesign::Fillet] Fillet017
  Base = -> Fillet016 [Edge52,Edge47,Edge11,Edge12,Edge1,Edge2,Edge6,Edge101,Edge115,Edge114,Edge133,Edge66,Edge64,Edge65,Edge67]
  BaseFeature = -> Fillet016
  Placement = pos=(0,0,0) rot=(1,0,0;1.5708rad)
  Radius = 1.5
  SupportTransform = false
  UseAllEdges = false
FEATURE [PartDesign::Fillet] Fillet018
  Base = -> Fillet017 [Edge103,Edge87,Edge185,Edge184,Edge183,Edge157]
  BaseFeature = -> Fillet017
  Placement = pos=(0,0,0) rot=(1,0,0;1.5708rad)
  Radius = 0.45
  SupportTransform = false
  UseAllEdges = false
FEATURE [PartDesign::Fillet] Fillet019
  Base = -> Fillet018 [Face53,Face54,Face55,Face49,Face50,Face51,Face45,Face46,Face47,Face25,Face26,Face23,Face29,Face30,Face27,Face33,Face34,Face31,Face52,Face32,Face28,Face48,Face44,Face24]
  BaseFeature = -> Fillet018
  Placement = pos=(0,0,0) rot=(1,0,0;1.5708rad)
  Radius = 0.5
  SupportTransform = false
  UseAllEdges = false
FEATURE [PartDesign::Fillet] Fillet020
  Base = -> Fillet019 [Face87,Face85,Face86]
  BaseFeature = -> Fillet019
  Placement = pos=(0,0,0) rot=(1,0,0;1.5708rad)
  Radius = 0.5
  SupportTransform = false
  UseAllEdges = false
FEATURE [PartDesign::Body] Body019  label="Body-v3.1_slicer"
  Group = -> [Sketch086,Pad034,Sketch087,Pad035,Mirrored002,Sketch088,Pad036,Sketch089,Pad037,Sketch092,Pad038,Sketch093,Pocket042,Fillet014,Fillet015,Fillet016,Fillet017,Fillet018,Fillet019,Fillet020]
  Origin = -> Origin018
  Placement = pos=(-280,59,161.477) rot=(0,0,1;0rad)
  Tip = -> Fillet020
COMPONENT P18 — recipe-attached ("Body-bearing002", modeled in this document).
Construction recipe (the document's own serialized feature program — sketch geometry with constraints, then the solid features built on it; lengths are millimeters unless a unit is written):

FEATURE [Sketcher::SketchObject] Sketch096
  FullyConstrained = true
  MapMode = 5
  Support = -> [XY_Plane019]
  sketch-geometry (2):
    g0: Circle CenterX=0 CenterY=0 CenterZ=0 NormalX=0 NormalY=0 NormalZ=1 AngleXU=0 Radius=3.95
    g1: Circle CenterX=0 CenterY=0 CenterZ=0 NormalX=0 NormalY=0 NormalZ=1 AngleXU=0 Radius=11
  constraints (4):
    c: Coincident(g0,g-1)
    c: Coincident(g1,g0)
    c: Diameter(g0) = 7.9
    c: Diameter(g1) = 22
FEATURE [PartDesign::Pad] Pad040
  Direction = (0,0,1)
  Length = 7
  Length2 = 10
  Profile = -> Sketch096
  ReferenceAxis = -> Sketch096 [N_Axis]
  Type = 0
FEATURE [PartDesign::Body] Body020  label="Body-bearing002"
  Group = -> [Sketch096,Pad040]
  Origin = -> Origin019
  Placement = pos=(-3.26004,-190.15,15.02) rot=(0,-1,0;1.5708rad)
  Tip = -> Pad040
COMPONENT P19 — recipe-attached ("slicer003", modeled in this document).
Construction recipe (the document's own serialized feature program — sketch geometry with constraints, then the solid features built on it; lengths are millimeters unless a unit is written):

FEATURE [Sketcher::SketchObject] Sketch097
  FullyConstrained = true
  MapMode = 5
  Support = -> [XY_Plane020]
  sketch-geometry (12):
    g0: LineSegment StartX=0 StartY=0 StartZ=0 EndX=40 EndY=0 EndZ=0
    g1: LineSegment StartX=40 StartY=0 StartZ=0 EndX=40 EndY=-104 EndZ=0
    g2: LineSegment StartX=40 StartY=-104 StartZ=0 EndX=0 EndY=-104 EndZ=0
    g3: LineSegment StartX=0 StartY=-104 StartZ=0 EndX=0 EndY=0 EndZ=0
    g4: LineSegment StartX=0 StartY=0 StartZ=0 EndX=5 EndY=6 EndZ=0
    g5: LineSegment StartX=5 StartY=6 StartZ=0 EndX=10 EndY=0 EndZ=0
    g6: LineSegment StartX=10 StartY=0 StartZ=0 EndX=15 EndY=6 EndZ=0
    g7: LineSegment StartX=15 StartY=6 StartZ=0 EndX=20 EndY=0 EndZ=0
    g8: LineSegment StartX=20 StartY=0 StartZ=0 EndX=25 EndY=6 EndZ=0
    g9: LineSegment StartX=25 StartY=6 StartZ=0 EndX=30 EndY=0 EndZ=0
    g10: LineSegment StartX=30 StartY=0 StartZ=0 EndX=35 EndY=6 EndZ=0
    g11: LineSegment StartX=35 StartY=6 StartZ=0 EndX=40 EndY=0 EndZ=0
  constraints (34):
    c: Coincident(g0,g1)
    c: Coincident(g1,g2)
    c: Coincident(g2,g3)
    c: Coincident(g3,g0)
    c: Horizontal(g0)
    c: Horizontal(g2)
    c: Vertical(g1)
    c: Vertical(g3)
    c: Coincident(g0,g-1)
    c: Coincident(g4,g0)
    c: Coincident(g5,g4)
    c: PointOnObject(g5,g0)
    c: Coincident(g6,g5)
    c: Coincident(g7,g6)
    c: PointOnObject(g7,g0)
    c: Coincident(g8,g7)
    c: Coincident(g9,g8)
    c: PointOnObject(g9,g0)
    c: Coincident(g10,g9)
    c: Coincident(g11,g10)
    c: Coincident(g11,g0)
    c: Horizontal(g4,g6)
    c: Horizontal(g6,g8)
    c: Horizontal(g8,g10)
    c: Equal(g4,g5)
    c: Equal(g5,g6)
    c: Equal(g6,g7)
    c: Equal(g7,g8)
    c: Equal(g8,g9)
    c: Equal(g9,g10)
    c: Equal(g10,g11)
    c: DistanceY(g3,g4) = 6
    c: DistanceY(g3,g3) = 104
    c: DistanceX(g2,g2) = 40
FEATURE [PartDesign::Pad] Pad041
  Direction = (0,0,1)
  Length = 100
  Length2 = 10
  Profile = -> Sketch097
  ReferenceAxis = -> Sketch097 [N_Axis]
  Type = 0
FEATURE [PartDesign::Body] Body021  label="slicer003"
  Group = -> [Sketch097,Pad041]
  Origin = -> Origin020
  Placement = pos=(-17,-110,-3.233e-12) rot=(0,0,1;0rad)
  Tip = -> Pad041
COMPONENT P20 — recipe-attached ("Body-v3.1_slicer001", modeled in this document).
Construction recipe (the document's own serialized feature program — sketch geometry with constraints, then the solid features built on it; lengths are millimeters unless a unit is written):

FEATURE [Sketcher::SketchObject] Sketch102
  FullyConstrained = true
  MapMode = 5
  Placement = pos=(0,0,0) rot=(1,0,0;1.5708rad)
  Support = -> [XZ_Plane021]
  sketch-geometry (16):
    g0: LineSegment StartX=-3.8476e-12 StartY=-10.8333 StartZ=0 EndX=4 EndY=-10.8333 EndZ=0
    g1: LineSegment StartX=4 StartY=-10.8333 StartZ=0 EndX=4 EndY=-0.833334 EndZ=0
    g2: LineSegment StartX=4 StartY=-0.833334 StartZ=0 EndX=-15 EndY=-0.833334 EndZ=0
    g3: LineSegment StartX=-15 StartY=-0.833334 StartZ=0 EndX=-15 EndY=0.833334 EndZ=0
    g4: LineSegment StartX=-15 StartY=0.833334 StartZ=0 EndX=4 EndY=0.833334 EndZ=0
    g5: LineSegment StartX=4 StartY=0.833334 StartZ=0 EndX=4 EndY=10.8333 EndZ=0
    g6: LineSegment StartX=4 StartY=10.8333 StartZ=0 EndX=0 EndY=10.8333 EndZ=0
    g7: LineSegment StartX=0 StartY=10.8333 StartZ=0 EndX=0 EndY=0.853333 EndZ=0
    g8: LineSegment StartX=0 StartY=0.853333 StartZ=0 EndX=-19 EndY=0.853333 EndZ=0
    g9: LineSegment StartX=-19 StartY=0.853333 StartZ=0 EndX=-19 EndY=-0.853333 EndZ=0
    g10: LineSegment StartX=-19 StartY=-0.853333 StartZ=0 EndX=-3.8476e-12 EndY=-0.853333 EndZ=0
    g11: LineSegment StartX=-3.8476e-12 StartY=-0.853333 StartZ=0 EndX=-3.8476e-12 EndY=-10.8333 EndZ=0
    g12: LineSegment StartX=-19 StartY=0.853333 StartZ=0 EndX=-15 EndY=-0.833334 EndZ=0
    g13: LineSegment StartX=-15 StartY=0.833334 StartZ=0 EndX=-19 EndY=-0.853333 EndZ=0
    g14: LineSegment StartX=0 StartY=0.853333 StartZ=0 EndX=0 EndY=0 EndZ=0
    g15: LineSegment StartX=0 StartY=0 StartZ=0 EndX=-3.8476e-12 EndY=-0.853333 EndZ=0
  constraints (44):
    c: Horizontal(g0)
    c: Coincident(g1,g0)
    c: Vertical(g1)
    c: Coincident(g2,g1)
    c: Horizontal(g2)
    c: Coincident(g3,g2)
    c: Vertical(g3)
    c: Horizontal(g4)
    c: Coincident(g5,g4)
    c: Vertical(g5)
    c: Coincident(g6,g5)
    c: PointOnObject(g6,g-2)
    c: Horizontal(g6)
    c: Coincident(g7,g6)
    c: Vertical(g7)
    c: Coincident(g8,g7)
    c: Horizontal(g8)
    c: Coincident(g9,g8)
    c: Vertical(g9)
    c: Coincident(g10,g9)
    c: Horizontal(g10)
    c: Coincident(g11,g10)
    c: Vertical(g11)
    c: DistanceY(g3,g3) = 1.66667
    c: Coincident(g3,g4)
    c: DistanceY(g9,g9) = 1.70667
    c: Coincident(g12,g8)
    c: Coincident(g12,g2)
    c: Coincident(g13,g3)
    c: Coincident(g13,g9)
    c: Equal(g13,g12)
    c: DistanceX(g9,g2) = 4
    c: DistanceX(g0,g0) = 4
    c: Equal(g0,g6)
    c: Equal(g1,g5)
    c: DistanceY(g1,g1) = 10
    c: DistanceX(g2,g10) = 15
    c: Coincident(g11,g0)
    c: Vertical(g1,g4)
    c: Coincident(g14,g7)
    c: Coincident(g14,g-1)
    c: Coincident(g15,g14)
    c: Coincident(g15,g10)
    c: Equal(g15,g14)
FEATURE [PartDesign::Pad] Pad043  label="Pad-main_body002"
  Direction = (0,-1,-2e-16)
  Length = 93
  Length2 = 10
  Placement = pos=(0,0,0) rot=(1,0,0;1.5708rad)
  Profile = -> Sketch102
  ReferenceAxis = -> Sketch102 [N_Axis]
  Type = 0
FEATURE [Sketcher::SketchObject] Sketch103
  ExternalGeometry = -> [Pad043]
  FullyConstrained = true
  MapMode = 5
  Placement = pos=(0,2e-16,0.853333) rot=(0,0,1;3.14159rad)
  Support = -> [Pad043]
  sketch-geometry (14):
    g0: ArcOfCircle CenterX=5.5 CenterY=23 CenterZ=0 NormalX=0 NormalY=0 NormalZ=1 AngleXU=0 Radius=1.7 StartAngle=1.5708 EndAngle=4.71239
    g1: ArcOfCircle CenterX=11.5 CenterY=23 CenterZ=0 NormalX=0 NormalY=0 NormalZ=1 AngleXU=0 Radius=1.7 StartAngle=4.71239 EndAngle=7.85398
    g2: LineSegment StartX=5.5 StartY=21.3 StartZ=0 EndX=11.5 EndY=21.3 EndZ=0
    g3: LineSegment StartX=11.5 StartY=24.7 StartZ=0 EndX=5.5 EndY=24.7 EndZ=0
    g4: ArcOfCircle CenterX=5.5 CenterY=48 CenterZ=0 NormalX=0 NormalY=0 NormalZ=1 AngleXU=0 Radius=1.7 StartAngle=1.5708 EndAngle=4.71239
    g5: ArcOfCircle CenterX=11.5 CenterY=48 CenterZ=0 NormalX=0 NormalY=0 NormalZ=1 AngleXU=0 Radius=1.7 StartAngle=4.71239 EndAngle=7.85398
    g6: LineSegment StartX=5.5 StartY=46.3 StartZ=0 EndX=11.5 EndY=46.3 EndZ=0
    g7: LineSegment StartX=11.5 StartY=49.7 StartZ=0 EndX=5.5 EndY=49.7 EndZ=0
    g8: ArcOfCircle CenterX=5.5 CenterY=73 CenterZ=0 NormalX=0 NormalY=0 NormalZ=1 AngleXU=0 Radius=1.7 StartAngle=1.5708 EndAngle=4.71239
    g9: ArcOfCircle CenterX=11.5 CenterY=73 CenterZ=0 NormalX=0 NormalY=0 NormalZ=1 AngleXU=0 Radius=1.7 StartAngle=4.71239 EndAngle=7.85398
    g10: LineSegment StartX=5.5 StartY=71.3 StartZ=0 EndX=11.5 EndY=71.3 EndZ=0
    g11: LineSegment StartX=11.5 StartY=74.7 StartZ=0 EndX=5.5 EndY=74.7 EndZ=0
    g12: LineSegment StartX=11.5 StartY=73 StartZ=0 EndX=11.5 EndY=48 EndZ=0
    g13: LineSegment StartX=11.5 StartY=48 StartZ=0 EndX=11.5 EndY=23 EndZ=0
  constraints (34):
    c: Tangent(g0,g2) = -1.5708
    c: Tangent(g2,g1) = -1.5708
    c: Tangent(g1,g3) = -1.5708
    c: Tangent(g3,g0) = -1.5708
    c: Equal(g0,g1)
    c: Horizontal(g2)
    c: Diameter(g1) = 3.4
    c: DistanceX(g2,g2) = 6
    c: DistanceX(g1,g-3) = 7.5
    c: Tangent(g4,g6) = -1.5708
    c: Tangent(g6,g5) = -1.5708
    c: Tangent(g5,g7) = -1.5708
    c: Tangent(g7,g4) = -1.5708
    c: Equal(g4,g5)
    c: Tangent(g8,g10) = -1.5708
    c: Tangent(g10,g9) = -1.5708
    c: Tangent(g9,g11) = -1.5708
    c: Tangent(g11,g8) = -1.5708
    c: Equal(g8,g9)
    c: Equal(g9,g5)
    c: Equal(g5,g1)
    c: Horizontal(g5,g4)
    c: Horizontal(g9,g8)
    c: Vertical(g8,g4)
    c: Vertical(g4,g0)
    c: Coincident(g12,g9)
    c: Coincident(g12,g5)
    c: Vertical(g12)
    c: Coincident(g13,g5)
    c: Coincident(g13,g1)
    c: Vertical(g13)
    c: Equal(g12,g13)
    c: DistanceY(g12,g12) = 25
    c: DistanceY(g9,g-3) = 20
FEATURE [PartDesign::Pad] Pad044  label="Pad-slots002"
  BaseFeature = -> Pad043
  Direction = (0,-2e-16,1)
  Length = 10
  Length2 = 10
  Placement = pos=(0,0,0) rot=(1,0,0;1.5708rad)
  Profile = -> Sketch103
  ReferenceAxis = -> Sketch103 [N_Axis]
  Type = 0
FEATURE [PartDesign::Mirrored] Mirrored006  label="Mirrored-slots_top_to_bottom002"
  BaseFeature = -> Pad044
  MirrorPlane = -> XY_Plane021
  Originals = -> [Pad044]
  Placement = pos=(0,0,0) rot=(1,0,0;1.5708rad)
FEATURE [Sketcher::SketchObject] Sketch104
  ExternalGeometry = -> [Mirrored006]
  FullyConstrained = true
  MapMode = 5
  Placement = pos=(0,-2e-16,-0.833334) rot=(0,0,1;3.14159rad)
  Support = -> [Mirrored006]
  sketch-geometry (5):
    g0: Circle CenterX=7.5 CenterY=23 CenterZ=0 NormalX=0 NormalY=0 NormalZ=1 AngleXU=0 Radius=1.69
    g1: Circle CenterX=7.5 CenterY=48 CenterZ=0 NormalX=0 NormalY=0 NormalZ=1 AngleXU=0 Radius=1.69
    g2: Circle CenterX=7.5 CenterY=73 CenterZ=0 NormalX=0 NormalY=0 NormalZ=1 AngleXU=0 Radius=1.69
    g3: LineSegment StartX=7.5 StartY=73 StartZ=0 EndX=7.5 EndY=48 EndZ=0
    g4: LineSegment StartX=7.5 StartY=48 StartZ=0 EndX=7.5 EndY=23 EndZ=0
  constraints (13):
    c: Equal(g2,g1)
    c: Equal(g2,g0)
    c: Diameter(g2) = 3.38
    c: Coincident(g3,g2)
    c: Coincident(g3,g1)
    c: Vertical(g3)
    c: Coincident(g4,g1)
    c: Coincident(g4,g0)
    c: Vertical(g4)
    c: DistanceY(g3,g3) = 25
    c: DistanceX(g0,g-3) = 7.5
    c: Equal(g3,g4)
    c: DistanceY(g2,g-3) = 20
FEATURE [PartDesign::Pad] Pad045  label="Pad-inside_holes002"
  BaseFeature = -> Mirrored006
  Direction = (0,-2e-16,1)
  Length = 10
  Length2 = 10
  Placement = pos=(0,0,0) rot=(1,0,0;1.5708rad)
  Profile = -> Sketch104
  ReferenceAxis = -> Sketch104 [N_Axis]
  Type = 0
FEATURE [Sketcher::SketchObject] Sketch105
  FullyConstrained = true
  MapMode = 5
  Placement = pos=(0,0,0) rot=(0.707107,0,-0.707107;3.14159rad)
  Support = -> [Pad045]
  sketch-geometry (1):
    g0: Circle CenterX=0 CenterY=3 CenterZ=0 NormalX=0 NormalY=0 NormalZ=1 AngleXU=0 Radius=4.55
  constraints (3):
    c: PointOnObject(g0,g-2)
    c: Diameter(g0) = 9.1
    c: DistanceY(g-1,g0) = 3
FEATURE [PartDesign::Pad] Pad046  label="Pad-shaft_female001"
  BaseFeature = -> Pad045
  Direction = (-1,0,-2e-16)
  Length = 19
  Length2 = 10
  Placement = pos=(0,0,0) rot=(1,0,0;1.5708rad)
  Profile = -> Sketch105
  ReferenceAxis = -> Sketch105 [N_Axis]
  Type = 0
FEATURE [Sketcher::SketchObject] Sketch106
  ExternalGeometry = -> [Pad046]
  FullyConstrained = true
  MapMode = 5
  Placement = pos=(0,0,0) rot=(-1,0,0;1.5708rad)
  Support = -> [Pad046]
  sketch-geometry (4):
    g0: LineSegment StartX=-3.8476e-12 StartY=10.8333 StartZ=0 EndX=4 EndY=10.8333 EndZ=0
    g1: LineSegment StartX=4 StartY=10.8333 StartZ=0 EndX=4 EndY=-10.8333 EndZ=0
    g2: LineSegment StartX=4 StartY=-10.8333 StartZ=0 EndX=-3.8476e-12 EndY=-10.8333 EndZ=0
    g3: LineSegment StartX=-3.8476e-12 StartY=-10.8333 StartZ=0 EndX=-3.8476e-12 EndY=10.8333 EndZ=0
  constraints (10):
    c: Coincident(g0,g1)
    c: Coincident(g1,g2)
    c: Coincident(g2,g3)
    c: Coincident(g3,g0)
    c: Horizontal(g0)
    c: Horizontal(g2)
    c: Vertical(g1)
    c: Vertical(g3)
    c: Coincident(g0,g-3)
    c: Coincident(g1,g-4)
FEATURE [PartDesign::Pad] Pad047  label="Pad-gap_extension001"
  BaseFeature = -> Pad046
  Direction = (0,1,2e-16)
  Length = 10
  Length2 = 10
  Placement = pos=(0,0,0) rot=(1,0,0;1.5708rad)
  Profile = -> Sketch106
  ReferenceAxis = -> Sketch106 [N_Axis]
  Type = 0
FEATURE [Sketcher::SketchObject] Sketch107
  ExternalGeometry = -> [Pad047]
  FullyConstrained = true
  MapMode = 5
  Placement = pos=(4,0,0) rot=(0.707107,0,0.707107;3.14159rad)
  Support = -> [Pad047]
  sketch-geometry (6):
    g0: ArcOfCircle CenterX=0 CenterY=3 CenterZ=0 NormalX=0 NormalY=0 NormalZ=1 AngleXU=0 Radius=4.5 StartAngle=1.75706 EndAngle=7.66772
    g1: GeomPoint X=-0.833334 Y=7.42217 Z=0
    g2: GeomPoint X=0.833334 Y=7.42217 Z=0
    g3: LineSegment StartX=-0.833334 StartY=7.42217 StartZ=0 EndX=-0.833334 EndY=8.42217 EndZ=0
    g4: LineSegment StartX=-0.833334 StartY=8.42217 StartZ=0 EndX=0.833334 EndY=8.42217 EndZ=0
    g5: LineSegment StartX=0.833334 StartY=8.42217 StartZ=0 EndX=0.833334 EndY=7.42217 EndZ=0
  constraints (15):
    c: PointOnObject(g0,g-2)
    c: DistanceY(g0) = 3
    c: Diameter(g0) = 9
    c: PointOnObject(g1,g-3)
    c: PointOnObject(g2,g-4)
    c: Coincident(g3,g1)
    c: PointOnObject(g3,g-3)
    c: Coincident(g4,g3)
    c: PointOnObject(g4,g-4)
    c: Horizontal(g4)
    c: Coincident(g5,g4)
    c: Coincident(g5,g2)
    c: Coincident(g0,g5)
    c: Coincident(g0,g3)
    c: DistanceY(g5,g5) = 1
FEATURE [PartDesign::Pocket] Pocket054  label="Pocket-shaft_male001"
  BaseFeature = -> Pad047
  Direction = (-1,0,2e-16)
  Length = 19
  Length2 = 5
  Placement = pos=(0,0,0) rot=(1,0,0;1.5708rad)
  Profile = -> Sketch107
  ReferenceAxis = -> Sketch107 [N_Axis]
  Type = 0
FEATURE [PartDesign::Fillet] Fillet035
  Base = -> Pocket054 [Edge69,Edge125,Edge59,Edge64,Edge62]
  BaseFeature = -> Pocket054
  Placement = pos=(0,0,0) rot=(1,0,0;1.5708rad)
  Radius = 0.45
  SupportTransform = false
  UseAllEdges = false
FEATURE [PartDesign::Fillet] Fillet036
  Base = -> Fillet035 [Edge64,Edge42]
  BaseFeature = -> Fillet035
  Placement = pos=(0,0,0) rot=(1,0,0;1.5708rad)
  Radius = 1
  SupportTransform = false
  UseAllEdges = false
FEATURE [PartDesign::Fillet] Fillet037
  Base = -> Fillet036 [Edge140,Edge141,Edge138,Edge132]
  BaseFeature = -> Fillet036
  Placement = pos=(0,0,0) rot=(1,0,0;1.5708rad)
  Radius = 1
  SupportTransform = false
  UseAllEdges = false
FEATURE [PartDesign::Fillet] Fillet038
  Base = -> Fillet037 [Edge52,Edge47,Edge11,Edge12,Edge1,Edge2,Edge6,Edge101,Edge115,Edge114,Edge133,Edge66,Edge64,Edge65,Edge67]
  BaseFeature = -> Fillet037
  Placement = pos=(0,0,0) rot=(1,0,0;1.5708rad)
  Radius = 1.5
  SupportTransform = false
  UseAllEdges = false
FEATURE [PartDesign::Fillet] Fillet039
  Base = -> Fillet038 [Edge103,Edge87,Edge185,Edge184,Edge183,Edge157]
  BaseFeature = -> Fillet038
  Placement = pos=(0,0,0) rot=(1,0,0;1.5708rad)
  Radius = 0.45
  SupportTransform = false
  UseAllEdges = false
FEATURE [PartDesign::Fillet] Fillet040
  Base = -> Fillet039 [Face53,Face54,Face55,Face49,Face50,Face51,Face45,Face46,Face47,Face25,Face26,Face23,Face29,Face30,Face27,Face33,Face34,Face31,Face52,Face32,Face28,Face48,Face44,Face24]
  BaseFeature = -> Fillet039
  Placement = pos=(0,0,0) rot=(1,0,0;1.5708rad)
  Radius = 0.5
  SupportTransform = false
  UseAllEdges = false
FEATURE [PartDesign::Fillet] Fillet041
  Base = -> Fillet040 [Face87,Face85,Face86]
  BaseFeature = -> Fillet040
  Placement = pos=(0,0,0) rot=(1,0,0;1.5708rad)
  Radius = 0.5
  SupportTransform = false
  UseAllEdges = false
FEATURE [PartDesign::Body] Body022  label="Body-v3.1_slicer001"
  Group = -> [Sketch102,Pad043,Sketch103,Pad044,Mirrored006,Sketch104,Pad045,Sketch105,Pad046,Sketch106,Pad047,Sketch107,Pocket054,Fillet035,Fillet036,Fillet037,Fillet038,Fillet039,Fillet040,Fillet041]
  Origin = -> Origin021
  Placement = pos=(-93.7453,-9.38195,-38.8423) rot=(-0.511946,0.823177,-0.245541;2.96464rad)
  Tip = -> Fillet041
COMPONENT P21 — recipe-attached ("Body-bearing003", modeled in this document).
Construction recipe (the document's own serialized feature program — sketch geometry with constraints, then the solid features built on it; lengths are millimeters unless a unit is written):

FEATURE [Sketcher::SketchObject] Sketch112
  FullyConstrained = true
  MapMode = 5
  Support = -> [XY_Plane022]
  sketch-geometry (2):
    g0: Circle CenterX=0 CenterY=0 CenterZ=0 NormalX=0 NormalY=0 NormalZ=1 AngleXU=0 Radius=3.95
    g1: Circle CenterX=0 CenterY=0 CenterZ=0 NormalX=0 NormalY=0 NormalZ=1 AngleXU=0 Radius=11
  constraints (4):
    c: Coincident(g0,g-1)
    c: Coincident(g1,g0)
    c: Diameter(g0) = 7.9
    c: Diameter(g1) = 22
FEATURE [PartDesign::Pad] Pad050
  Direction = (0,0,1)
  Length = 7
  Length2 = 10
  Profile = -> Sketch112
  ReferenceAxis = -> Sketch112 [N_Axis]
  Type = 0
FEATURE [PartDesign::Body] Body023  label="Body-bearing003"
  Group = -> [Sketch112,Pad050]
  Origin = -> Origin022
  Placement = pos=(-125.413,-93.1724,-47.4092) rot=(0.443141,-0.743648,0.500613;1.76697rad)
  Tip = -> Pad050
COMPONENT P22 — recipe-attached ("Body_M3_20mm", modeled in this document).
Construction recipe (the document's own serialized feature program — sketch geometry with constraints, then the solid features built on it; lengths are millimeters unless a unit is written):

FEATURE [Sketcher::SketchObject] Sketch119
  FullyConstrained = true
  MapMode = 5
  Support = -> [XY_Plane023]
  sketch-geometry (1):
    g0: Circle CenterX=0 CenterY=0 CenterZ=0 NormalX=0 NormalY=0 NormalZ=1 AngleXU=0 Radius=2.675
  constraints (2):
    c: Coincident(g0,g-1)
    c: Diameter(g0) = 5.35
FEATURE [PartDesign::Pad] Pad054
  Direction = (0,0,1)
  Length = 2.9
  Length2 = 10
  Profile = -> Sketch119
  ReferenceAxis = -> Sketch119 [N_Axis]
  Type = 0
FEATURE [Sketcher::SketchObject] Sketch120
  FullyConstrained = true
  MapMode = 5
  Placement = pos=(0,0,2.9) rot=(0,0,1;0rad)
  Support = -> [Pad054]
  sketch-geometry (1):
    g0: Circle CenterX=0 CenterY=0 CenterZ=0 NormalX=0 NormalY=0 NormalZ=1 AngleXU=0 Radius=1.465
  constraints (2):
    c: Coincident(g0,g-1)
    c: Diameter(g0) = 2.93
FEATURE [PartDesign::Pad] Pad055
  BaseFeature = -> Pad054
  Direction = (0,0,1)
  Length = 20
  Length2 = 10
  Profile = -> Sketch120
  ReferenceAxis = -> Sketch120 [N_Axis]
  Type = 0
FEATURE [Sketcher::SketchObject] Sketch121
  FullyConstrained = true
  MapMode = 5
  Placement = pos=(0,0,0) rot=(1,0,0;3.14159rad)
  Support = -> [Pad055]
  sketch-geometry (7):
    g0: LineSegment StartX=1.20378 StartY=0.695 StartZ=0 EndX=0 EndY=1.39 EndZ=0
    g1: LineSegment StartX=0 StartY=1.39 StartZ=0 EndX=-1.20378 EndY=0.695 EndZ=0
    g2: LineSegment StartX=-1.20378 StartY=0.695 StartZ=0 EndX=-1.20378 EndY=-0.695 EndZ=0
    g3: LineSegment StartX=-1.20378 StartY=-0.695 StartZ=0 EndX=1.122e-12 EndY=-1.39 EndZ=0
    g4: LineSegment StartX=1.122e-12 StartY=-1.39 StartZ=0 EndX=1.20378 EndY=-0.695 EndZ=0
    g5: LineSegment StartX=1.20378 StartY=-0.695 StartZ=0 EndX=1.20378 EndY=0.695 EndZ=0
    g6: Circle CenterX=0 CenterY=0 CenterZ=0 NormalX=0 NormalY=0 NormalZ=1 AngleXU=0 Radius=1.39
  constraints (16):
    c: Coincident(g0,g1)
    c: Coincident(g1,g2)
    c: Coincident(g2,g3)
    c: Coincident(g3,g4)
    c: Coincident(g4,g5)
    c: Coincident(g5,g0)
    c: Equal(g0, g1-g5) x5
    c: PointOnObject(g0,g6)
    c: PointOnObject(g1,g6)
    c: PointOnObject(g2,g6)
    c: PointOnObject(g3,g6)
    c: PointOnObject(g4,g6)
    c: PointOnObject(g5,g6)
    c: Coincident(g6,g-1)
    c: Vertical(g6,g0)
    c: Diameter(g6) = 2.78
FEATURE [PartDesign::Pocket] Pocket060
  BaseFeature = -> Pad055
  Direction = (0,0,1)
  Length = 1.94
  Length2 = 5
  Profile = -> Sketch121
  ReferenceAxis = -> Sketch121 [N_Axis]
  Type = 0
FEATURE [PartDesign::Body] Body024  label="Body_M3_20mm"
  Group = -> [Sketch119,Pad054,Sketch120,Pad055,Sketch121,Pocket060]
  Origin = -> Origin023
  Placement = pos=(-136.273,-95.5019,-27.2393) rot=(-0.915728,-0.020525,-0.401274;1.89287rad)
  Tip = -> Pocket060
COMPONENT P23 — recipe-attached ("Body-bearing_retainer_slicer", modeled in this document).
Construction recipe (the document's own serialized feature program — sketch geometry with constraints, then the solid features built on it; lengths are millimeters unless a unit is written):

FEATURE [Sketcher::SketchObject] Sketch122
  FullyConstrained = true
  MapMode = 5
  Support = -> [XY_Plane024]
  sketch-geometry (4):
    g0: LineSegment StartX=0 StartY=0 StartZ=0 EndX=2 EndY=0 EndZ=0
    g1: LineSegment StartX=2 StartY=0 StartZ=0 EndX=2 EndY=-20 EndZ=0
    g2: LineSegment StartX=2 StartY=-20 StartZ=0 EndX=0 EndY=-20 EndZ=0
    g3: LineSegment StartX=0 StartY=-20 StartZ=0 EndX=0 EndY=0 EndZ=0
  constraints (11):
    c: Coincident(g0,g1)
    c: Coincident(g1,g2)
    c: Coincident(g2,g3)
    c: Coincident(g3,g0)
    c: Horizontal(g0)
    c: Horizontal(g2)
    c: Vertical(g1)
    c: Vertical(g3)
    c: Coincident(g0,g-1)
    c: DistanceX(g2,g2) = 2
    c: DistanceY(g3,g3) = 20
FEATURE [PartDesign::Pad] Pad056
  Direction = (0,0,1)
  Length = 20
  Length2 = 10
  Profile = -> Sketch122
  ReferenceAxis = -> Sketch122 [N_Axis]
  Type = 0
FEATURE [PartDesign::Body] Body025  label="Body-bearing_retainer_slicer"
  Group = -> [Sketch122,Pad056]
  Origin = -> Origin024
  Placement = pos=(-140.26,-89.9499,-43.1962) rot=(-0.427271,-0.154361,0.890849;1.21892rad)
  Tip = -> Pad056
COMPONENT P24 — recipe-attached ("Body026", modeled in this document).
Construction recipe (the document's own serialized feature program — sketch geometry with constraints, then the solid features built on it; lengths are millimeters unless a unit is written):

FEATURE [Sketcher::SketchObject] Sketch126
  FullyConstrained = true
  MapMode = 5
  Placement = pos=(0,0,0) rot=(0.57735,0.57735,0.57735;2.0944rad)
  Support = -> [YZ_Plane025]
  sketch-geometry (4):
    g0: LineSegment StartX=0 StartY=0 StartZ=0 EndX=60 EndY=0 EndZ=0
    g1: LineSegment StartX=60 StartY=0 StartZ=0 EndX=60 EndY=20 EndZ=0
    g2: LineSegment StartX=60 StartY=20 StartZ=0 EndX=0 EndY=20 EndZ=0
    g3: LineSegment StartX=0 StartY=20 StartZ=0 EndX=0 EndY=0 EndZ=0
  constraints (11):
    c: Coincident(g0,g1)
    c: Coincident(g1,g2)
    c: Coincident(g2,g3)
    c: Horizontal(g0)
    c: Horizontal(g2)
    c: Vertical(g1)
    c: Vertical(g3)
    c: DistanceY(g1,g1) = 20
    c: DistanceX(g0,g0) = 60
    c: Coincident(g0,g3)
    c: Coincident(g0,g-1)
FEATURE [PartDesign::Pad] Pad058
  Direction = (1,-2e-16,3e-16)
  Length = 8
  Length2 = 10
  Placement = pos=(0,0,0) rot=(0.57735,0.57735,0.57735;2.0944rad)
  Profile = -> Sketch126
  ReferenceAxis = -> Sketch126 [N_Axis]
  Type = 0
FEATURE [Sketcher::SketchObject] Sketch127
  FullyConstrained = true
  MapMode = 5
  Placement = pos=(0,0,0) rot=(-0.57735,-0.57735,0.57735;4.18879rad)
  Support = -> [Pad058]
  sketch-geometry (4):
    g0: LineSegment StartX=0 StartY=0 StartZ=0 EndX=-60 EndY=0 EndZ=0
    g1: LineSegment StartX=-60 StartY=0 StartZ=0 EndX=-60 EndY=20 EndZ=0
    g2: LineSegment StartX=-60 StartY=20 StartZ=0 EndX=0 EndY=20 EndZ=0
    g3: LineSegment StartX=0 StartY=20 StartZ=0 EndX=0 EndY=0 EndZ=0
  constraints (11):
    c: Coincident(g0,g1)
    c: Coincident(g1,g2)
    c: Coincident(g2,g3)
    c: Coincident(g3,g0)
    c: Horizontal(g0)
    c: Horizontal(g2)
    c: Vertical(g1)
    c: Vertical(g3)
    c: Coincident(g0,g-1)
    c: DistanceX(g2,g2) = 60
    c: DistanceY(g3,g3) = 20
FEATURE [PartDesign::Pad] Pad059
  BaseFeature = -> Pad058
  Direction = (-4e-16,-1,2e-16)
  Length = 10
  Length2 = 10
  Placement = pos=(0,0,0) rot=(0.57735,0.57735,0.57735;2.0944rad)
  Profile = -> Sketch127
  ReferenceAxis = -> Sketch127 [N_Axis]
  Reversed = true
  Type = 0
FEATURE [Sketcher::SketchObject] Sketch128
  ExternalGeometry = -> [Pad059]
  FullyConstrained = true
  MapMode = 5
  Placement = pos=(0,0,0) rot=(0.57735,0.57735,-0.57735;4.18879rad)
  Support = -> [Pad059]
  sketch-geometry (5):
    g0: LineSegment StartX=10 StartY=-60 StartZ=0 EndX=60 EndY=-20 EndZ=0
    g1: LineSegment StartX=60 StartY=-20 StartZ=0 EndX=43.9922 EndY=-20 EndZ=0
    g2: LineSegment StartX=43.9922 StartY=-20 StartZ=0 EndX=10 EndY=-47.1938 EndZ=0
    g3: LineSegment StartX=10 StartY=-47.1938 StartZ=0 EndX=10 EndY=-60 EndZ=0
    g4: LineSegment StartX=25 StartY=-35.1938 StartZ=0 EndX=31.247 EndY=-43.0024 EndZ=0
  constraints (14):
    c: Coincident(g0,g-4)
    c: Coincident(g0,g-3)
    c: Coincident(g1,g0)
    c: PointOnObject(g1,g-3)
    c: Coincident(g2,g1)
    c: PointOnObject(g2,g-4)
    c: Coincident(g3,g2)
    c: Coincident(g3,g0)
    c: Parallel(g2,g0)
    c: PointOnObject(g4,g2)
    c: PointOnObject(g4,g0)
    c: Angle(g0,g4) = 1.5708
    c: Distance(g4) = 10
    c: DistanceX(g4) = 25
FEATURE [PartDesign::Pad] Pad060
  BaseFeature = -> Pad059
  Direction = (-1,6e-16,-5e-16)
  Length = 4
  Length2 = 10
  Placement = pos=(0,0,0) rot=(0.57735,0.57735,0.57735;2.0944rad)
  Profile = -> Sketch128
  ReferenceAxis = -> Sketch128 [N_Axis]
  Reversed = true
  Type = 0
FEATURE [Sketcher::SketchObject] Sketch129
  ExternalGeometry = -> [Pad060]
  FullyConstrained = true
  MapMode = 5
  Placement = pos=(8,-1.8e-15,1.8e-15) rot=(0.57735,0.57735,0.57735;2.0944rad)
  Support = -> [Pad060]
  sketch-geometry (7):
    g0: ArcOfCircle CenterX=22.5 CenterY=10 CenterZ=0 NormalX=0 NormalY=0 NormalZ=1 AngleXU=0 Radius=6 StartAngle=1.5708 EndAngle=4.71239
    g1: ArcOfCircle CenterX=47.5 CenterY=10 CenterZ=0 NormalX=0 NormalY=0 NormalZ=1 AngleXU=0 Radius=6 StartAngle=4.71239 EndAngle=7.85398
    g2: LineSegment StartX=22.5 StartY=4 StartZ=0 EndX=47.5 EndY=4 EndZ=0
    g3: LineSegment StartX=47.5 StartY=16 StartZ=0 EndX=22.5 EndY=16 EndZ=0
    g4: LineSegment StartX=47.5 StartY=10 StartZ=0 EndX=60 EndY=20 EndZ=0
    g5: LineSegment StartX=10 StartY=20 StartZ=0 EndX=22.5 EndY=10 EndZ=0
    g6: LineSegment StartX=22.5 StartY=10 StartZ=0 EndX=10 EndY=-5.3e-15 EndZ=0
  constraints (16):
    c: Tangent(g0,g2) = -1.5708
    c: Tangent(g2,g1) = -1.5708
    c: Tangent(g1,g3) = -1.5708
    c: Tangent(g3,g0) = -1.5708
    c: Equal(g0,g1)
    c: Horizontal(g2)
    c: Coincident(g4,g1)
    c: Coincident(g4,g-3)
    c: DistanceX(g2,g2) = 25
    c: Diameter(g1) = 12
    c: Coincident(g5,g-5)
    c: Coincident(g5,g0)
    c: Coincident(g6,g0)
    c: Coincident(g6,g-5)
    c: Equal(g5,g6)
    c: Equal(g6,g4)
FEATURE [PartDesign::Pocket] Pocket063
  BaseFeature = -> Pad060
  Direction = (-1,8e-16,-6e-16)
  Length = 5
  Length2 = 5
  Placement = pos=(0,0,0) rot=(0.57735,0.57735,0.57735;2.0944rad)
  Profile = -> Sketch129
  ReferenceAxis = -> Sketch129 [N_Axis]
  Type = 0
FEATURE [Sketcher::SketchObject] Sketch133
  ExternalGeometry = -> [Pocket063]
  FullyConstrained = true
  MapMode = 5
  Placement = pos=(4.4e-15,10,-1.7e-15) rot=(0.57735,0.57735,0.57735;4.18879rad)
  Support = -> [Pocket063]
  sketch-geometry (7):
    g0: ArcOfCircle CenterX=27.5 CenterY=10 CenterZ=0 NormalX=0 NormalY=0 NormalZ=1 AngleXU=0 Radius=6 StartAngle=1.5708 EndAngle=4.71239
    g1: ArcOfCircle CenterX=52.5 CenterY=10 CenterZ=0 NormalX=0 NormalY=0 NormalZ=1 AngleXU=0 Radius=6 StartAngle=4.71239 EndAngle=7.85398
    g2: LineSegment StartX=27.5 StartY=4 StartZ=0 EndX=52.5 EndY=4 EndZ=0
    g3: LineSegment StartX=52.5 StartY=16 StartZ=0 EndX=27.5 EndY=16 EndZ=0
    g4: LineSegment StartX=52.5 StartY=10 StartZ=0 EndX=60 EndY=20 EndZ=0
    g5: LineSegment StartX=60 StartY=-5.72e-14 StartZ=0 EndX=52.5 EndY=10 EndZ=0
    g6: LineSegment StartX=27.5 StartY=10 StartZ=0 EndX=20 EndY=-2.49e-14 EndZ=0
  constraints (16):
    c: Tangent(g0,g2) = -1.5708
    c: Tangent(g2,g1) = -1.5708
    c: Tangent(g1,g3) = -1.5708
    c: Tangent(g3,g0) = -1.5708
    c: Equal(g0,g1)
    c: Horizontal(g2)
    c: DistanceX(g2,g2) = 25
    c: Diameter(g1) = 12
    c: Coincident(g4,g1)
    c: Coincident(g4,g-3)
    c: Coincident(g5,g1)
    c: Coincident(g6,g0)
    c: Coincident(g6,g-5)
    c: Equal(g5,g4)
    c: Equal(g4,g6)
    c: Coincident(g5,g-4)
FEATURE [PartDesign::Pocket] Pocket064
  BaseFeature = -> Pocket063
  Direction = (-4e-16,-1,1.1e-15)
  Length = 5
  Length2 = 5
  Placement = pos=(0,0,0) rot=(0.57735,0.57735,0.57735;2.0944rad)
  Profile = -> Sketch133
  ReferenceAxis = -> Sketch133 [N_Axis]
  Type = 0
FEATURE [PartDesign::Chamfer] Chamfer007
  Angle = 45
  Base = -> Pocket064 [Edge13]
  BaseFeature = -> Pocket064
  ChamferType = 0
  FlipDirection = false
  Placement = pos=(0,0,0) rot=(0.57735,0.57735,0.57735;2.0944rad)
  Size = 6
  Size2 = 1
  SupportTransform = false
  UseAllEdges = false
FEATURE [PartDesign::Fillet] Fillet049
  Base = -> Chamfer007 [Edge44,Edge35]
  BaseFeature = -> Chamfer007
  Placement = pos=(0,0,0) rot=(0.57735,0.57735,0.57735;2.0944rad)
  Radius = 9
  SupportTransform = false
  UseAllEdges = false
FEATURE [PartDesign::Fillet] Fillet050
  Base = -> Fillet049 [Edge23]
  BaseFeature = -> Fillet049
  Placement = pos=(0,0,0) rot=(0.57735,0.57735,0.57735;2.0944rad)
  Radius = 19
  SupportTransform = false
  UseAllEdges = false
FEATURE [PartDesign::Fillet] Fillet051
  Base = -> Fillet050 [Edge32]
  BaseFeature = -> Fillet050
  Placement = pos=(0,0,0) rot=(0.57735,0.57735,0.57735;2.0944rad)
  Radius = 5
  SupportTransform = false
  UseAllEdges = false
FEATURE [PartDesign::Fillet] Fillet052
  Base = -> Fillet051 [Edge33,Edge35]
  BaseFeature = -> Fillet051
  Placement = pos=(0,0,0) rot=(0.57735,0.57735,0.57735;2.0944rad)
  Radius = 1
  SupportTransform = false
  UseAllEdges = false
FEATURE [PartDesign::Fillet] Fillet053
  Base = -> Fillet052 [Edge57,Edge15]
  BaseFeature = -> Fillet052
  Placement = pos=(0,0,0) rot=(0.57735,0.57735,0.57735;2.0944rad)
  Radius = 3
  SupportTransform = false
  UseAllEdges = false
FEATURE [PartDesign::Fillet] Fillet054
  Base = -> Fillet053 [Edge77]
  BaseFeature = -> Fillet053
  Placement = pos=(0,0,0) rot=(0.57735,0.57735,0.57735;2.0944rad)
  Radius = 9
  SupportTransform = false
  UseAllEdges = false
FEATURE [PartDesign::Fillet] Fillet055
  Base = -> Fillet054 [Face29,Face28,Face30,Face15]
  BaseFeature = -> Fillet054
  Placement = pos=(0,0,0) rot=(0.57735,0.57735,0.57735;2.0944rad)
  Radius = 1
  SupportTransform = false
  UseAllEdges = false
FEATURE [PartDesign::Fillet] Fillet056
  Base = -> Fillet055 [Face4,Face10,Face6,Face8]
  BaseFeature = -> Fillet055
  Placement = pos=(0,0,0) rot=(0.57735,0.57735,0.57735;2.0944rad)
  Radius = 0.5
  SupportTransform = false
  UseAllEdges = false
FEATURE [PartDesign::Fillet] Fillet057
  Base = -> Fillet056 [Edge60]
  BaseFeature = -> Fillet056
  Placement = pos=(0,0,0) rot=(0.57735,0.57735,0.57735;2.0944rad)
  Radius = 0.5
  SupportTransform = false
  UseAllEdges = false
FEATURE [PartDesign::Fillet] Fillet058
  Base = -> Fillet057 [Face27,Face50]
  BaseFeature = -> Fillet057
  Placement = pos=(0,0,0) rot=(0.57735,0.57735,0.57735;2.0944rad)
  Radius = 0.5
  SupportTransform = false
  UseAllEdges = false
FEATURE [PartDesign::Fillet] Fillet059
  Base = -> Fillet058 [Face77,Face76,Face74,Face75]
  BaseFeature = -> Fillet058
  Placement = pos=(0,0,0) rot=(0.57735,0.57735,0.57735;2.0944rad)
  Radius = 0.5
  SupportTransform = false
  UseAllEdges = false
FEATURE [Sketcher::SketchObject] Sketch134
  ExternalGeometry = -> [Fillet059]
  FullyConstrained = true
  MapMode = 5
  Placement = pos=(2.2e-15,5,-5.3e-15) rot=(0.57735,0.57735,0.57735;4.18879rad)
  Support = -> [Fillet059]
  sketch-geometry (2):
    g0: Circle CenterX=27.5 CenterY=10 CenterZ=0 NormalX=0 NormalY=0 NormalZ=1 AngleXU=0 Radius=3.15
    g1: Circle CenterX=52.5 CenterY=10 CenterZ=0 NormalX=0 NormalY=0 NormalZ=1 AngleXU=0 Radius=3.15
  constraints (4):
    c: Coincident(g0,g-3)
    c: Coincident(g1,g-4)
    c: Equal(g0,g1)
    c: Diameter(g0) = 6.3
FEATURE [PartDesign::Pocket] Pocket065
  BaseFeature = -> Fillet059
  Direction = (-5e-16,-1,1.4e-15)
  Length = 5
  Length2 = 5
  Placement = pos=(0,0,0) rot=(0.57735,0.57735,0.57735;2.0944rad)
  Profile = -> Sketch134
  ReferenceAxis = -> Sketch134 [N_Axis]
  Type = 0
FEATURE [Sketcher::SketchObject] Sketch135
  ExternalGeometry = -> [Pocket065]
  FullyConstrained = true
  MapMode = 5
  Placement = pos=(3,-2.1e-15,1.7e-15) rot=(0.57735,0.57735,0.57735;2.0944rad)
  Support = -> [Pocket065]
  sketch-geometry (2):
    g0: Circle CenterX=22.5 CenterY=10 CenterZ=0 NormalX=0 NormalY=0 NormalZ=1 AngleXU=0 Radius=3.15
    g1: Circle CenterX=47.5 CenterY=10 CenterZ=0 NormalX=0 NormalY=0 NormalZ=1 AngleXU=0 Radius=3.15
  constraints (4):
    c: Coincident(g0,g-3)
    c: Coincident(g1,g-4)
    c: Equal(g1,g0)
    c: Diameter(g0) = 6.3
FEATURE [PartDesign::Pocket] Pocket066
  BaseFeature = -> Pocket065
  Direction = (-1,1.3e-15,-9e-16)
  Length = 5
  Length2 = 5
  Placement = pos=(0,0,0) rot=(0.57735,0.57735,0.57735;2.0944rad)
  Profile = -> Sketch135
  ReferenceAxis = -> Sketch135 [N_Axis]
  Type = 0
FEATURE [PartDesign::Body] Body026
  Group = -> [Sketch126,Pad058,Sketch127,Pad059,Sketch128,Pad060,Sketch129,Pocket063,Sketch133,Pocket064,Chamfer007,Fillet049,Fillet050,Fillet051,Fillet052,Fillet053,Fillet054,Fillet055,Fillet056,Fillet057,Fillet058,Fillet059,Sketch134,Pocket065,Sketch135,Pocket066]
  Origin = -> Origin025
  Tip = -> Pocket066
COMPONENT P25 — recipe-attached ("Body026002", modeled in this document).
Construction recipe (the document's own serialized feature program — sketch geometry with constraints, then the solid features built on it; lengths are millimeters unless a unit is written):

FEATURE [Sketcher::SketchObject] Sketch197
  FullyConstrained = true
  MapMode = 5
  Placement = pos=(0,0,0) rot=(0.57735,0.57735,0.57735;2.0944rad)
  Support = -> [YZ_Plane037]
  sketch-geometry (4):
    g0: LineSegment StartX=0 StartY=0 StartZ=0 EndX=31 EndY=0 EndZ=0
    g1: LineSegment StartX=31 StartY=0 StartZ=0 EndX=31 EndY=65 EndZ=0
    g2: LineSegment StartX=31 StartY=65 StartZ=0 EndX=0 EndY=65 EndZ=0
    g3: LineSegment StartX=0 StartY=65 StartZ=0 EndX=0 EndY=0 EndZ=0
  constraints (11):
    c: Coincident(g0,g1)
    c: Coincident(g1,g2)
    c: Coincident(g2,g3)
    c: Coincident(g3,g0)
    c: Horizontal(g0)
    c: Horizontal(g2)
    c: Vertical(g1)
    c: Vertical(g3)
    c: Coincident(g0,g-1)
    c: DistanceY(g1,g1) = 65
    c: DistanceX(g2,g2) = 31
FEATURE [PartDesign::Pad] Pad101  label="Pad101-servo_bracket_body"
  Direction = (1,-2e-16,3e-16)
  Length = 4
  Length2 = 10
  Placement = pos=(0,0,0) rot=(0.57735,0.57735,0.57735;2.0944rad)
  Profile = -> Sketch197
  ReferenceAxis = -> Sketch197 [N_Axis]
  Type = 0
FEATURE [Sketcher::SketchObject] Sketch198
  ExternalGeometry = -> [Pad101]
  FullyConstrained = true
  MapMode = 5
  Placement = pos=(0,1e-16,0) rot=(-0.57735,-0.57735,0.57735;4.18879rad)
  Support = -> [Pad101]
  sketch-geometry (7):
    g0: LineSegment StartX=-77 StartY=8.5 StartZ=0 EndX=12 EndY=8.5 EndZ=0
    g1: LineSegment StartX=12 StartY=-9.5 StartZ=0 EndX=-77 EndY=-9.5 EndZ=0
    g2: LineSegment StartX=-77 StartY=6.5 StartZ=0 EndX=12 EndY=6.5 EndZ=0
    g3: LineSegment StartX=12 StartY=8.5 StartZ=0 EndX=12 EndY=6.5 EndZ=0
    g4: LineSegment StartX=12 StartY=6.5 StartZ=0 EndX=12 EndY=-9.5 EndZ=0
    g5: LineSegment StartX=-77 StartY=-9.5 StartZ=0 EndX=-77 EndY=6.5 EndZ=0
    g6: LineSegment StartX=-77 StartY=6.5 StartZ=0 EndX=-77 EndY=8.5 EndZ=0
  constraints (20):
    c: Coincident(g0,g3)
    c: Coincident(g4,g1)
    c: Coincident(g1,g5)
    c: Coincident(g6,g0)
    c: Horizontal(g0)
    c: Horizontal(g1)
    c: DistanceX(g4) = 12
    c: DistanceX(g1,g-3) = 12
    c: DistanceY(g-3,g0) = 4.5
    c: Horizontal(g2)
    c: DistanceY(g2,g0) = 2
    c: Coincident(g3,g4)
    c: Vertical(g3)
    c: Vertical(g4)
    c: Coincident(g2,g3)
    c: Coincident(g5,g6)
    c: Vertical(g5)
    c: Vertical(g6)
    c: Coincident(g2,g5)
    c: DistanceY(g4,g4) = 16
FEATURE [PartDesign::Pad] Pad102  label="Pad102-rail_mount_body"
  BaseFeature = -> Pad101
  Direction = (-4e-16,-1,2e-16)
  Length = 4
  Length2 = 10
  Placement = pos=(0,0,0) rot=(0.57735,0.57735,0.57735;2.0944rad)
  Profile = -> Sketch198
  ReferenceAxis = -> Sketch198 [N_Axis]
  Reversed = true
  Type = 0
FEATURE [Sketcher::SketchObject] Sketch199
  ExternalGeometry = -> [Pad102]
  FullyConstrained = true
  MapMode = 5
  Placement = pos=(0,0,0) rot=(0.57735,0.57735,-0.57735;4.18879rad)
  Support = -> [Pad102]
  sketch-geometry (17):
    g0: LineSegment StartX=4 StartY=-11.5 StartZ=0 EndX=25 EndY=-11.5 EndZ=0
    g1: LineSegment StartX=25 StartY=-11.5 StartZ=0 EndX=25 EndY=-53.5 EndZ=0
    g2: LineSegment StartX=25 StartY=-53.5 StartZ=0 EndX=4 EndY=-53.5 EndZ=0
    g3: LineSegment StartX=4 StartY=-53.5 StartZ=0 EndX=4 EndY=-11.5 EndZ=0
    g4: LineSegment StartX=4 StartY=-11.5 StartZ=0 EndX=4 EndY=0 EndZ=0
    g5: LineSegment StartX=4 StartY=-65 StartZ=0 EndX=4 EndY=-53.5 EndZ=0
    g6: Circle CenterX=9.6 CenterY=-8.275 CenterZ=0 NormalX=0 NormalY=0 NormalZ=1 AngleXU=0 Radius=1.125
    g7: Circle CenterX=19.4 CenterY=-8.275 CenterZ=0 NormalX=0 NormalY=0 NormalZ=1 AngleXU=0 Radius=1.125
    g8: Circle CenterX=9.6 CenterY=-56.725 CenterZ=0 NormalX=0 NormalY=0 NormalZ=1 AngleXU=0 Radius=1.125
    g9: Circle CenterX=19.4 CenterY=-56.725 CenterZ=0 NormalX=0 NormalY=0 NormalZ=1 AngleXU=0 Radius=1.125
    g10: LineSegment StartX=9.6 StartY=-8.275 StartZ=0 EndX=19.4 EndY=-8.275 EndZ=0
    g11: LineSegment StartX=19.4 StartY=-8.275 StartZ=0 EndX=19.4 EndY=-56.725 EndZ=0
    g12: LineSegment StartX=19.4 StartY=-56.725 StartZ=0 EndX=9.6 EndY=-56.725 EndZ=0
    g13: LineSegment StartX=9.6 StartY=-56.725 StartZ=0 EndX=9.6 EndY=-8.275 EndZ=0
    g14: LineSegment StartX=9.6 StartY=-56.725 StartZ=0 EndX=4 EndY=-53.5 EndZ=0
    g15: LineSegment StartX=25 StartY=-53.5 StartZ=0 EndX=19.4 EndY=-56.725 EndZ=0
    g16: LineSegment StartX=19.4 StartY=-8.275 StartZ=0 EndX=25 EndY=-11.5 EndZ=0
  constraints (42):
    c: Coincident(g0,g1)
    c: Coincident(g1,g2)
    c: Coincident(g2,g3)
    c: Coincident(g3,g0)
    c: Horizontal(g0)
    c: Horizontal(g2)
    c: Vertical(g1)
    c: Vertical(g3)
    c: PointOnObject(g0,g-3)
    c: DistanceX(g0,g0) = 21
    c: DistanceY(g1,g1) = 42
    c: Coincident(g4,g0)
    c: Coincident(g4,g-3)
    c: Coincident(g5,g-3)
    c: Coincident(g5,g2)
    c: Equal(g5,g4)
    c: Equal(g8,g9)
    c: Equal(g9,g6)
    c: Equal(g6,g7)
    c: Diameter(g7) = 2.25
    c: Coincident(g10,g6)
    c: Coincident(g10,g7)
    c: Horizontal(g10)
    c: Coincident(g11,g7)
    c: Coincident(g11,g9)
    c: Vertical(g11)
    c: Coincident(g12,g9)
    c: Coincident(g12,g8)
    c: Horizontal(g12)
    c: Coincident(g13,g8)
    c: Coincident(g13,g6)
    c: Vertical(g13)
    c: Coincident(g14,g8)
    c: Coincident(g14,g2)
    c: Coincident(g15,g1)
    c: Coincident(g15,g9)
    c: Coincident(g16,g7)
    c: Coincident(g16,g0)
    c: Equal(g16,g15)
    c: Equal(g15,g14)
    c: DistanceY(g11,g11) = 48.45
    c: DistanceX(g12,g12) = 9.8
FEATURE [PartDesign::Pocket] Pocket090  label="Pocket090-servo_slot_and_holes"
  BaseFeature = -> Pad102
  Direction = (1,-6e-16,5e-16)
  Length = 5
  Length2 = 5
  Placement = pos=(0,0,0) rot=(0.57735,0.57735,0.57735;2.0944rad)
  Profile = -> Sketch199
  ReferenceAxis = -> Sketch199 [N_Axis]
  Type = 0
FEATURE [Sketcher::SketchObject] Sketch200
  ExternalGeometry = -> [Pocket090]
  FullyConstrained = true
  MapMode = 5
  Placement = pos=(0,0,0) rot=(0.57735,0.57735,-0.57735;4.18879rad)
  Support = -> [Pocket090]
  sketch-geometry (9):
    g0: LineSegment StartX=13.5 StartY=-53.5 StartZ=0 EndX=15.5 EndY=-53.5 EndZ=0
    g1: LineSegment StartX=15.5 StartY=-53.5 StartZ=0 EndX=15.5 EndY=-60.5 EndZ=0
    g2: LineSegment StartX=15.5 StartY=-60.5 StartZ=0 EndX=13.5 EndY=-60.5 EndZ=0
    g3: LineSegment StartX=13.5 StartY=-60.5 StartZ=0 EndX=13.5 EndY=-53.5 EndZ=0
    g4: LineSegment StartX=13.5 StartY=-11.5 StartZ=0 EndX=15.5 EndY=-11.5 EndZ=0
    g5: LineSegment StartX=15.5 StartY=-11.5 StartZ=0 EndX=15.5 EndY=-4.5 EndZ=0
    g6: LineSegment StartX=15.5 StartY=-4.5 StartZ=0 EndX=13.5 EndY=-4.5 EndZ=0
    g7: LineSegment StartX=13.5 StartY=-4.5 StartZ=0 EndX=13.5 EndY=-11.5 EndZ=0
    g8: GeomPoint X=14.5 Y=-11.5 Z=0
  constraints (24):
    c: Coincident(g0,g1)
    c: Coincident(g1,g2)
    c: Coincident(g2,g3)
    c: Coincident(g3,g0)
    c: Horizontal(g0)
    c: Horizontal(g2)
    c: Vertical(g1)
    c: Vertical(g3)
    c: PointOnObject(g0,g-4)
    c: Coincident(g4,g5)
    c: Coincident(g5,g6)
    c: Coincident(g6,g7)
    c: Coincident(g7,g4)
    c: Horizontal(g4)
    c: Horizontal(g6)
    c: Vertical(g5)
    c: Vertical(g7)
    c: Symmetric(g4,g4,g8)
    c: Symmetric(g-3,g-3,g8)
    c: Vertical(g0,g4)
    c: Vertical(g4,g0)
    c: DistanceX(g6,g6) = 2
    c: Equal(g5,g1)
    c: DistanceY(g5,g5) = 7
FEATURE [PartDesign::Pocket] Pocket091  label="Pocket091-servo_cantilever_slot"
  BaseFeature = -> Pocket090
  Direction = (1,-8e-16,7e-16)
  Length = 1.75
  Length2 = 5
  Placement = pos=(0,0,0) rot=(0.57735,0.57735,0.57735;2.0944rad)
  Profile = -> Sketch200
  ReferenceAxis = -> Sketch200 [N_Axis]
  Type = 0
FEATURE [Sketcher::SketchObject] Sketch201
  ExternalGeometry = -> [Pocket091]
  FullyConstrained = true
  MapMode = 5
  Placement = pos=(1.8e-15,4,-7e-16) rot=(0.57735,0.57735,0.57735;4.18879rad)
  Support = -> [Pocket091]
  sketch-geometry (6):
    g0: Circle CenterX=71 CenterY=-1.5 CenterZ=0 NormalX=0 NormalY=0 NormalZ=1 AngleXU=0 Radius=3.1
    g1: Circle CenterX=-6 CenterY=-1.5 CenterZ=0 NormalX=0 NormalY=0 NormalZ=1 AngleXU=0 Radius=3.1
    g2: LineSegment StartX=-6 StartY=-1.5 StartZ=0 EndX=-12 EndY=-9.5 EndZ=0
    g3: LineSegment StartX=71 StartY=-1.5 StartZ=0 EndX=77 EndY=-9.5 EndZ=0
    g4: LineSegment StartX=71 StartY=-1.5 StartZ=0 EndX=77 EndY=6.5 EndZ=0
    g5: LineSegment StartX=-12 StartY=6.5 StartZ=0 EndX=-6 EndY=-1.5 EndZ=0
  constraints (14):
    c: Equal(g1,g0)
    c: DistanceX(g-4,g1) = 6
    c: Coincident(g2,g1)
    c: Coincident(g2,g-4)
    c: Coincident(g3,g0)
    c: Coincident(g3,g-3)
    c: Coincident(g4,g0)
    c: Coincident(g4,g-3)
    c: Equal(g2,g3)
    c: Equal(g3,g4)
    c: Diameter(g0) = 6.2
    c: Coincident(g5,g-4)
    c: Coincident(g5,g1)
    c: Equal(g2,g5)
FEATURE [PartDesign::Pocket] Pocket092  label="Pocket092-mount_holes"
  BaseFeature = -> Pocket091
  Direction = (-4e-16,-1,1.1e-15)
  Length = 5
  Length2 = 5
  Placement = pos=(0,0,0) rot=(0.57735,0.57735,0.57735;2.0944rad)
  Profile = -> Sketch201
  ReferenceAxis = -> Sketch201 [N_Axis]
  Type = 0
FEATURE [PartDesign::Fillet] Fillet093  label="Fillet093-mount_plate"
  Base = -> Pocket092 [Edge12,Edge16,Edge11,Edge14]
  BaseFeature = -> Pocket092
  Placement = pos=(0,0,0) rot=(0.57735,0.57735,0.57735;2.0944rad)
  Radius = 7.5
  SupportTransform = false
  UseAllEdges = false
FEATURE [PartDesign::Fillet] Fillet094  label="Fillet094-servo_plate"
  Base = -> Fillet093 [Edge77,Edge46]
  BaseFeature = -> Fillet093
  Placement = pos=(0,0,0) rot=(0.57735,0.57735,0.57735;2.0944rad)
  Radius = 11
  SupportTransform = false
  UseAllEdges = false
FEATURE [PartDesign::Fillet] Fillet095  label="Fillet095-mount_plate_surface"
  Base = -> Fillet094 [Face36]
  BaseFeature = -> Fillet094
  Placement = pos=(0,0,0) rot=(0.57735,0.57735,0.57735;2.0944rad)
  Radius = 1.2
  SupportTransform = false
  UseAllEdges = false
FEATURE [Sketcher::SketchObject] Sketch207
  ExternalGeometry = -> [Fillet095]
  FullyConstrained = true
  MapMode = 5
  Placement = pos=(0,0,0) rot=(0.57735,0.57735,-0.57735;4.18879rad)
  Support = -> [Fillet095]
  sketch-geometry (8):
    g0: LineSegment StartX=4 StartY=4e-15 StartZ=0 EndX=19 EndY=4e-15 EndZ=0
    g1: LineSegment StartX=19 StartY=4e-15 StartZ=0 EndX=19 EndY=-3 EndZ=0
    g2: LineSegment StartX=19 StartY=-3 StartZ=0 EndX=4 EndY=-3 EndZ=0
    g3: LineSegment StartX=4 StartY=-3 StartZ=0 EndX=4 EndY=4e-15 EndZ=0
    g4: LineSegment StartX=4 StartY=-62 StartZ=0 EndX=19 EndY=-62 EndZ=0
    g5: LineSegment StartX=19 StartY=-62 StartZ=0 EndX=19 EndY=-65 EndZ=0
    g6: LineSegment StartX=19 StartY=-65 StartZ=0 EndX=4 EndY=-65 EndZ=0
    g7: LineSegment StartX=4 StartY=-65 StartZ=0 EndX=4 EndY=-62 EndZ=0
  constraints (22):
    c: Coincident(g0,g1)
    c: Coincident(g1,g2)
    c: Coincident(g2,g3)
    c: Coincident(g3,g0)
    c: Horizontal(g0)
    c: Horizontal(g2)
    c: Vertical(g1)
    c: Vertical(g3)
    c: Coincident(g4,g5)
    c: Coincident(g5,g6)
    c: Coincident(g6,g7)
    c: Coincident(g7,g4)
    c: Horizontal(g4)
    c: Horizontal(g6)
    c: Vertical(g5)
    c: Vertical(g7)
    c: Equal(g5,g1)
    c: Equal(g2,g4)
    c: Coincident(g6,g-4)
    c: DistanceY(g5,g5) = 3
    c: DistanceX(g6,g6) = 15
    c: Coincident(g0,g-3)
FEATURE [PartDesign::Pad] Pad104  label="Pad104-cantilever"
  BaseFeature = -> Fillet095
  Direction = (-1,1.3e-15,-8e-16)
  Length = 8
  Length2 = 10
  Placement = pos=(0,0,0) rot=(0.57735,0.57735,0.57735;2.0944rad)
  Profile = -> Sketch207
  ReferenceAxis = -> Sketch207 [N_Axis]
  Type = 0
FEATURE [Sketcher::SketchObject] Sketch208
  ExternalGeometry = -> [Pad104]
  FullyConstrained = true
  MapMode = 5
  Placement = pos=(-5.07e-14,1.82e-14,65) rot=(0,0,-1;1.5708rad)
  Support = -> [Pad104]
  sketch-geometry (3):
    g0: LineSegment StartX=-19 StartY=-4.3e-14 StartZ=0 EndX=-4 EndY=-8 EndZ=0
    g1: LineSegment StartX=-19 StartY=-4.3e-14 StartZ=0 EndX=-19 EndY=-8 EndZ=0
    g2: LineSegment StartX=-19 StartY=-8 StartZ=0 EndX=-4 EndY=-8 EndZ=0
  constraints (6):
    c: Coincident(g0,g-3)
    c: Coincident(g0,g-4)
    c: Coincident(g1,g0)
    c: Coincident(g1,g-4)
    c: Coincident(g2,g1)
    c: Coincident(g2,g0)
FEATURE [PartDesign::Pocket] Pocket097  label="Pocket097-cantilever"
  BaseFeature = -> Pad104
  Direction = (9e-16,-4e-16,-1)
  Length = 5
  Length2 = 5
  Placement = pos=(0,0,0) rot=(0.57735,0.57735,0.57735;2.0944rad)
  Profile = -> Sketch208
  ReferenceAxis = -> Sketch208 [N_Axis]
  Type = 1
FEATURE [PartDesign::Fillet] Fillet096
  Base = -> Pocket097 [Edge31,Edge18]
  BaseFeature = -> Pocket097
  Placement = pos=(0,0,0) rot=(0.57735,0.57735,0.57735;2.0944rad)
  Radius = 0.5
  SupportTransform = false
  UseAllEdges = false
FEATURE [PartDesign::Fillet] Fillet097
  Base = -> Fillet096 [Edge114,Edge113,Edge98,Edge97,Edge124,Edge117,Edge105,Edge104,Edge68,Edge66,Edge67,Edge65]
  BaseFeature = -> Fillet096
  Placement = pos=(0,0,0) rot=(0.57735,0.57735,0.57735;2.0944rad)
  Radius = 0.5
  SupportTransform = false
  UseAllEdges = false
FEATURE [PartDesign::Body] Body026002
  Group = -> [Sketch197,Pad101,Sketch198,Pad102,Sketch199,Pocket090,Sketch200,Pocket091,Sketch201,Pocket092,Fillet093,Fillet094,Fillet095,Sketch207,Pad104,Sketch208,Pocket097,Fillet096,Fillet097]
  Origin = -> Origin036
  Tip = -> Fillet097
COMPONENT P26 — recipe-attached ("Body026003", modeled in this document).
Construction recipe (the document's own serialized feature program — sketch geometry with constraints, then the solid features built on it; lengths are millimeters unless a unit is written):

FEATURE [Sketcher::SketchObject] Sketch202
  FullyConstrained = true
  MapMode = 5
  Placement = pos=(0,0,0) rot=(0.57735,0.57735,0.57735;2.0944rad)
  Support = -> [YZ_Plane038]
  sketch-geometry (6):
    g0: LineSegment StartX=-50 StartY=-10 StartZ=0 EndX=-1.8181e-05 EndY=-10 EndZ=0
    g1: LineSegment StartX=-1.8181e-05 StartY=-10 StartZ=0 EndX=-1.8181e-05 EndY=10 EndZ=0
    g2: LineSegment StartX=-1.8181e-05 StartY=10 StartZ=0 EndX=-50 EndY=10 EndZ=0
    g3: LineSegment StartX=-50 StartY=10 StartZ=0 EndX=-50 EndY=-10 EndZ=0
    g4: ArcOfCircle CenterX=0 CenterY=0 CenterZ=0 NormalX=0 NormalY=0 NormalZ=1 AngleXU=0 Radius=10 StartAngle=4.71239 EndAngle=7.85398
    g5: Circle CenterX=0 CenterY=0 CenterZ=0 NormalX=0 NormalY=0 NormalZ=1 AngleXU=0 Radius=1.65
  constraints (16):
    c: Coincident(g0,g1)
    c: Coincident(g1,g2)
    c: Coincident(g2,g3)
    c: Coincident(g3,g0)
    c: Horizontal(g0)
    c: Horizontal(g2)
    c: Vertical(g1)
    c: Vertical(g3)
    c: Coincident(g4,g-1)
    c: Coincident(g4,g0)
    c: Coincident(g4,g1)
    c: Diameter(g4) = 20
    c: Coincident(g5,g4)
    c: Diameter(g5) = 3.3
    c: DistanceY(g3,g3) = 20
    c: DistanceX(g2) = -50
FEATURE [PartDesign::Pad] Pad103  label="Pad103-arm_body"
  Direction = (1,-2e-16,3e-16)
  Length = 8
  Length2 = 10
  Placement = pos=(0,0,0) rot=(0.57735,0.57735,0.57735;2.0944rad)
  Profile = -> Sketch202
  ReferenceAxis = -> Sketch202 [N_Axis]
  Type = 0
FEATURE [Sketcher::SketchObject] Sketch203
  ExternalGeometry = -> [Pad103]
  FullyConstrained = true
  MapMode = 5
  Placement = pos=(8,-1.8e-15,1.8e-15) rot=(0.57735,0.57735,0.57735;2.0944rad)
  Support = -> [Pad103]
  sketch-geometry (4):
    g0: ArcOfCircle CenterX=0 CenterY=10 CenterZ=0 NormalX=0 NormalY=0 NormalZ=1 AngleXU=0 Radius=45.4567 StartAngle=3.3634 EndAngle=3.59717
    g1: ArcOfCircle CenterX=-50 CenterY=2 CenterZ=0 NormalX=0 NormalY=0 NormalZ=1 AngleXU=0 Radius=6 StartAngle=5.94335 EndAngle=7.85398
    g2: LineSegment StartX=-50 StartY=8 StartZ=0 EndX=-50 EndY=-10 EndZ=0
    g3: LineSegment StartX=-50 StartY=-10 StartZ=0 EndX=-40.8205 EndY=-10 EndZ=0
  constraints (13):
    c: PointOnObject(g0,g-3)
    c: PointOnObject(g1,g-4)
    c: PointOnObject(g1,g-4)
    c: Coincident(g0,g1)
    c: PointOnObject(g0,g-2)
    c: DistanceY(g0) = 10
    c: Radius(g1) = 6
    c: DistanceY(g-4,g1) = 12
    c: PointOnObject(g0,g-1)
    c: Coincident(g2,g1)
    c: Coincident(g2,g-4)
    c: Coincident(g3,g2)
    c: Coincident(g3,g0)
FEATURE [PartDesign::Pocket] Pocket093  label="Pocket093-latch_cutout"
  BaseFeature = -> Pad103
  Direction = (-1,4e-16,-4e-16)
  Length = 5
  Length2 = 5
  Placement = pos=(0,0,0) rot=(0.57735,0.57735,0.57735;2.0944rad)
  Profile = -> Sketch203
  ReferenceAxis = -> Sketch203 [N_Axis]
  Type = 0
FEATURE [Sketcher::SketchObject] Sketch204
  FullyConstrained = true
  MapMode = 5
  Placement = pos=(0,0,0) rot=(0.57735,0.57735,-0.57735;4.18879rad)
  Support = -> [Pocket093]
  sketch-geometry (5):
    g0: LineSegment StartX=0 StartY=0 StartZ=0 EndX=0 EndY=3.1 EndZ=0
    g1: LineSegment StartX=0 StartY=3.1 StartZ=0 EndX=0.3384 EndY=2.67871 EndZ=0
    g2: LineSegment StartX=0.3384 StartY=2.67871 StartZ=0 EndX=0.770939 EndY=3.00261 EndZ=0
    g3: LineSegment StartX=0.770939 StartY=3.00261 StartZ=0 EndX=0 EndY=0 EndZ=0
    g4: LineSegment StartX=0.3384 StartY=2.67871 StartZ=0 EndX=0 EndY=0 EndZ=0
  constraints (13):
    c: Coincident(g0,g-1)
    c: PointOnObject(g0,g-2)
    c: Coincident(g1,g0)
    c: Coincident(g2,g1)
    c: Coincident(g3,g2)
    c: Coincident(g3,g0)
    c: Distance(g0) = 3.1
    c: Equal(g3,g0)
    c: Angle(g3,g0) = 0.251327
    c: Coincident(g4,g1)
    c: Coincident(g4,g0)
    c: Angle(g4,g0) = 0.125664
    c: Distance(g4) = 2.7
FEATURE [PartDesign::Pocket] Pocket094  label="Pocket094-spline"
  BaseFeature = -> Pocket093
  Direction = (1,-6e-16,5e-16)
  Length = 3.75
  Length2 = 5
  Placement = pos=(0,0,0) rot=(0.57735,0.57735,0.57735;2.0944rad)
  Profile = -> Sketch204
  ReferenceAxis = -> Sketch204 [N_Axis]
  Type = 0
FEATURE [PartDesign::PolarPattern] PolarPattern002
  Angle = 360
  Axis = -> X_Axis037
  BaseFeature = -> Pocket094
  Occurrences = 25
  Originals = -> [Pocket094]
  Placement = pos=(0,0,0) rot=(0.57735,0.57735,0.57735;2.0944rad)
FEATURE [Sketcher::SketchObject] Sketch205
  FullyConstrained = true
  MapMode = 5
  Placement = pos=(8,-1.8e-15,1.8e-15) rot=(0.57735,0.57735,0.57735;2.0944rad)
  Support = -> [PolarPattern002]
  sketch-geometry (1):
    g0: Circle CenterX=0 CenterY=0 CenterZ=0 NormalX=0 NormalY=0 NormalZ=1 AngleXU=0 Radius=3.25
  constraints (2):
    c: Coincident(g0,g-1)
    c: Diameter(g0) = 6.5
FEATURE [PartDesign::Pocket] Pocket095
  BaseFeature = -> PolarPattern002
  Direction = (-1,8e-16,-6e-16)
  Length = 2
  Length2 = 5
  Placement = pos=(0,0,0) rot=(0.57735,0.57735,0.57735;2.0944rad)
  Profile = -> Sketch205
  ReferenceAxis = -> Sketch205 [N_Axis]
  Type = 0
FEATURE [PartDesign::Fillet] Fillet091  label="Fillet091-screw_hole"
  Base = -> Pocket095 [Edge174]
  BaseFeature = -> Pocket095
  Placement = pos=(0,0,0) rot=(0.57735,0.57735,0.57735;2.0944rad)
  Radius = 0.45
  SupportTransform = false
  UseAllEdges = false
FEATURE [PartDesign::Fillet] Fillet092  label="Fillet092-spline"
  Base = -> Fillet091 [Face30,Face31,Face32,Face33,Face34,Face35,Face36,Face37,Face38,Face14,Face15,Face16,Face17,Face18,Face19,Face29,Face28,Face27,Face26,Face25,Face24,Face23,Face22,Face21,Face20]
  BaseFeature = -> Fillet091
  Placement = pos=(0,0,0) rot=(0.57735,0.57735,0.57735;2.0944rad)
  Radius = 0.1
  SupportTransform = false
  UseAllEdges = false
FEATURE [Sketcher::SketchObject] Sketch206
  ExternalGeometry = -> [Fillet092]
  FullyConstrained = true
  MapMode = 5
  Placement = pos=(8,-1.8e-15,1.8e-15) rot=(0.57735,0.57735,0.57735;2.0944rad)
  Support = -> [Fillet092]
  sketch-geometry (10):
    g0: LineSegment StartX=-8 StartY=1.46667 StartZ=0 EndX=-22 EndY=-6 EndZ=0
    g1: LineSegment StartX=-8 StartY=1.46667 StartZ=0 EndX=-8 EndY=-6 EndZ=0
    g2: LineSegment StartX=-8 StartY=-6 StartZ=0 EndX=-22 EndY=-6 EndZ=0
    g3: LineSegment StartX=-8 StartY=6 StartZ=0 EndX=-30.5 EndY=-6 EndZ=0
    g4: LineSegment StartX=-30.5 StartY=-6 StartZ=0 EndX=-30.5 EndY=6 EndZ=0
    g5: LineSegment StartX=-30.5 StartY=6 StartZ=0 EndX=-8 EndY=6 EndZ=0
    g6: LineSegment StartX=-34.5 StartY=-6 StartZ=0 EndX=-34.5 EndY=6 EndZ=0
    g7: LineSegment StartX=-34.5 StartY=6 StartZ=0 EndX=-39.5 EndY=6 EndZ=0
    g8: LineSegment StartX=-39.5 StartY=6 StartZ=0 EndX=-34.5 EndY=-6 EndZ=0
    g9: LineSegment StartX=-22 StartY=-6 StartZ=0 EndX=-23.8824 EndY=-2.47059 EndZ=0
  constraints (30):
    c: Coincident(g1,g0)
    c: Vertical(g1)
    c: Coincident(g2,g1)
    c: Coincident(g2,g0)
    c: Horizontal(g2)
    c: Coincident(g4,g3)
    c: Vertical(g4)
    c: Coincident(g5,g4)
    c: Coincident(g5,g3)
    c: Horizontal(g5)
    c: Vertical(g6)
    c: Coincident(g7,g6)
    c: Horizontal(g7)
    c: Coincident(g8,g7)
    c: Coincident(g8,g6)
    c: Horizontal(g6,g4)
    c: Horizontal(g0,g3)
    c: Horizontal(g3,g6)
    c: DistanceX(g6,g4) = 4
    c: Coincident(g9,g0)
    c: PointOnObject(g9,g3)
    c: Angle(g0,g9) = 1.5708
    c: Distance(g9) = 4
    c: Vertical(g0,g3)
    c: DistanceY(g-4,g1) = 4
    c: DistanceY(g3,g-3) = 4
    c: DistanceX(g5,g5) = 22.5
    c: DistanceX(g7,g7) = 5
    c: DistanceX(g1,g-1) = 8
    c: Angle(g9,g3) = 1.5708
FEATURE [PartDesign::Pocket] Pocket096
  BaseFeature = -> Fillet092
  Direction = (-1,1.1e-15,-7e-16)
  Length = 5
  Length2 = 5
  Placement = pos=(0,0,0) rot=(0.57735,0.57735,0.57735;2.0944rad)
  Profile = -> Sketch206
  ReferenceAxis = -> Sketch206 [N_Axis]
  Type = 1
FEATURE [PartDesign::Fillet] Fillet098
  Base = -> Pocket096 [Edge473,Edge471]
  BaseFeature = -> Pocket096
  Placement = pos=(0,0,0) rot=(0.57735,0.57735,0.57735;2.0944rad)
  Radius = 1
  SupportTransform = false
  UseAllEdges = false
FEATURE [PartDesign::Fillet] Fillet099
  Base = -> Fillet098 [Face1]
  BaseFeature = -> Fillet098
  Placement = pos=(0,0,0) rot=(0.57735,0.57735,0.57735;2.0944rad)
  Radius = 0.5
  SupportTransform = false
  UseAllEdges = false
FEATURE [PartDesign::Fillet] Fillet100
  Base = -> Fillet099 [Edge60]
  BaseFeature = -> Fillet099
  Placement = pos=(0,0,0) rot=(0.57735,0.57735,0.57735;2.0944rad)
  Radius = 2.5
  SupportTransform = false
  UseAllEdges = false
FEATURE [PartDesign::Fillet] Fillet101
  Base = -> Fillet100 [Face12]
  BaseFeature = -> Fillet100
  Placement = pos=(0,0,0) rot=(0.57735,0.57735,0.57735;2.0944rad)
  Radius = 0.25
  SupportTransform = false
  UseAllEdges = false
FEATURE [PartDesign::Fillet] Fillet102
  Base = -> Fillet101 [Face209]
  BaseFeature = -> Fillet101
  Placement = pos=(0,0,0) rot=(0.57735,0.57735,0.57735;2.0944rad)
  Radius = 0.2
  SupportTransform = false
  UseAllEdges = false
FEATURE [PartDesign::Body] Body026003
  Group = -> [Sketch202,Pad103,Sketch203,Pocket093,Sketch204,Pocket094,PolarPattern002,Sketch205,Pocket095,Fillet091,Fillet092,Sketch206,Pocket096,Fillet098,Fillet099,Fillet100,Fillet101,Fillet102]
  Origin = -> Origin037
  Tip = -> Fillet102
COMPONENT P27 — recipe-attached ("Body026004", modeled in this document).
Construction recipe (the document's own serialized feature program — sketch geometry with constraints, then the solid features built on it; lengths are millimeters unless a unit is written):

FEATURE [Sketcher::SketchObject] Sketch209
  FullyConstrained = false
  MapMode = 5
  Placement = pos=(0,0,0) rot=(1,0,0;1.5708rad)
  Support = -> [XZ_Plane038]
  sketch-geometry (4):
    g0: LineSegment StartX=0 StartY=0 StartZ=0 EndX=43.0754 EndY=0 EndZ=0
    g1: LineSegment StartX=43.0754 StartY=0 StartZ=0 EndX=43.0754 EndY=20.5261 EndZ=0
    g2: LineSegment StartX=43.0754 StartY=20.5261 StartZ=0 EndX=0 EndY=20.5261 EndZ=0
    g3: LineSegment StartX=0 StartY=20.5261 StartZ=0 EndX=0 EndY=0 EndZ=0
  constraints (9):
    c: Coincident(g0,g1)
    c: Coincident(g1,g2)
    c: Coincident(g2,g3)
    c: Coincident(g3,g0)
    c: Horizontal(g0)
    c: Horizontal(g2)
    c: Vertical(g1)
    c: Vertical(g3)
    c: Coincident(g0,g-1)
FEATURE [PartDesign::Pad] Pad105
  Direction = (0,-1,2e-16)
  Length = 10
  Length2 = 10
  Placement = pos=(0,0,0) rot=(1,0,0;1.5708rad)
  Profile = -> Sketch209
  ReferenceAxis = -> Sketch209 [N_Axis]
  Reversed = true
  Type = 0
FEATURE [PartDesign::Body] Body026004
  Group = -> [Sketch209,Pad105]
  Origin = -> Origin038
  Tip = -> Pad105
COMPONENT P28 — recipe-attached ("Body026005", modeled in this document).
Construction recipe (the document's own serialized feature program — sketch geometry with constraints, then the solid features built on it; lengths are millimeters unless a unit is written):

FEATURE [Sketcher::SketchObject] Sketch210
  FullyConstrained = true
  MapMode = 5
  Support = -> [XY_Plane039]
  sketch-geometry (4):
    g0: LineSegment StartX=0 StartY=0 StartZ=0 EndX=20 EndY=0 EndZ=0
    g1: LineSegment StartX=20 StartY=0 StartZ=0 EndX=20 EndY=-40 EndZ=0
    g2: LineSegment StartX=20 StartY=-40 StartZ=0 EndX=0 EndY=-40 EndZ=0
    g3: LineSegment StartX=0 StartY=-40 StartZ=0 EndX=0 EndY=0 EndZ=0
  constraints (11):
    c: Coincident(g0,g1)
    c: Coincident(g1,g2)
    c: Coincident(g2,g3)
    c: Coincident(g3,g0)
    c: Horizontal(g0)
    c: Horizontal(g2)
    c: Vertical(g1)
    c: Vertical(g3)
    c: Coincident(g0,g-1)
    c: DistanceX(g2,g2) = 20
    c: DistanceY(g1,g1) = 40
FEATURE [PartDesign::Pad] Pad106  label="Pad106-base"
  Direction = (0,0,1)
  Length = 6
  Length2 = 10
  Profile = -> Sketch210
  ReferenceAxis = -> Sketch210 [N_Axis]
  Type = 0
FEATURE [Sketcher::SketchObject] Sketch211
  ExternalGeometry = -> [Pad106]
  FullyConstrained = true
  MapMode = 5
  Placement = pos=(0,0,6) rot=(0,0,1;0rad)
  Support = -> [Pad106]
  sketch-geometry (5):
    g0: LineSegment StartX=0 StartY=-13.5 StartZ=0 EndX=8 EndY=-13.5 EndZ=0
    g1: LineSegment StartX=8 StartY=-13.5 StartZ=0 EndX=8 EndY=-26.5 EndZ=0
    g2: LineSegment StartX=8 StartY=-26.5 StartZ=0 EndX=0 EndY=-26.5 EndZ=0
    g3: LineSegment StartX=0 StartY=-26.5 StartZ=0 EndX=0 EndY=-13.5 EndZ=0
    g4: GeomPoint X=0 Y=-20 Z=0
  constraints (12):
    c: Coincident(g0,g1)
    c: Coincident(g1,g2)
    c: Coincident(g2,g3)
    c: Coincident(g3,g0)
    c: Horizontal(g0)
    c: Horizontal(g2)
    c: Vertical(g1)
    c: Vertical(g3)
    c: DistanceX(g2,g2) = 8
    c: DistanceY(g3,g3) = 13
    c: Symmetric(g3,g3,g4)
    c: Symmetric(g-3,g-3,g4)
FEATURE [PartDesign::Pad] Pad107  label="Pad107-vertical"
  BaseFeature = -> Pad106
  Direction = (0,0,1)
  Length = 20
  Length2 = 10
  Profile = -> Sketch211
  ReferenceAxis = -> Sketch211 [N_Axis]
  Type = 0
FEATURE [PartDesign::Fillet] Fillet103  label="Fillet103-base"
  Base = -> Pad107 [Edge5,Edge10,Edge1,Edge2]
  BaseFeature = -> Pad107
  Radius = 9
  SupportTransform = false
  UseAllEdges = false
FEATURE [PartDesign::Fillet] Fillet104  label="Fillet104-vertical"
  Base = -> Fillet103 [Edge36,Edge32]
  BaseFeature = -> Fillet103
  Radius = 6
  SupportTransform = false
  UseAllEdges = false
FEATURE [Sketcher::SketchObject] Sketch212
  ExternalGeometry = -> [Fillet104]
  FullyConstrained = true
  MapMode = 5
  Placement = pos=(0,0,6) rot=(0,0,1;0rad)
  Support = -> [Fillet104]
  sketch-geometry (5):
    g0: Circle CenterX=10 CenterY=-6 CenterZ=0 NormalX=0 NormalY=0 NormalZ=1 AngleXU=0 Radius=5
    g1: Circle CenterX=10 CenterY=-34 CenterZ=0 NormalX=0 NormalY=0 NormalZ=1 AngleXU=0 Radius=5
    g2: LineSegment StartX=9 StartY=0 StartZ=0 EndX=10 EndY=-6 EndZ=0
    g3: LineSegment StartX=10 StartY=-6 StartZ=0 EndX=11 EndY=0 EndZ=0
    g4: LineSegment StartX=10 StartY=-34 StartZ=0 EndX=9 EndY=-40 EndZ=0
  constraints (12):
    c: Vertical(g1,g0)
    c: Equal(g0,g1)
    c: Coincident(g2,g-3)
    c: Coincident(g2,g0)
    c: Coincident(g3,g0)
    c: Coincident(g3,g-3)
    c: Equal(g3,g2)
    c: Diameter(g0) = 10
    c: DistanceY(g0) = -6
    c: Coincident(g4,g1)
    c: Coincident(g4,g-4)
    c: Equal(g4,g2)
FEATURE [PartDesign::Pocket] Pocket098  label="Pocket098-horizontal_inset"
  BaseFeature = -> Fillet104
  Direction = (0,0,-1)
  Length = 3
  Length2 = 5
  Profile = -> Sketch212
  ReferenceAxis = -> Sketch212 [N_Axis]
  Type = 0
FEATURE [Sketcher::SketchObject] Sketch213
  ExternalGeometry = -> [Pocket098]
  FullyConstrained = true
  MapMode = 5
  Placement = pos=(0,0,0) rot=(0.57735,-0.57735,-0.57735;2.0944rad)
  Support = -> [Pocket098]
  sketch-geometry (3):
    g0: Circle CenterX=20 CenterY=19 CenterZ=0 NormalX=0 NormalY=0 NormalZ=1 AngleXU=0 Radius=5
    g1: LineSegment StartX=19.5 StartY=26 StartZ=0 EndX=20 EndY=19 EndZ=0
    g2: LineSegment StartX=20 StartY=19 StartZ=0 EndX=20.5 EndY=26 EndZ=0
  constraints (7):
    c: Diameter(g0) = 10
    c: Coincident(g1,g-3)
    c: Coincident(g1,g0)
    c: Coincident(g2,g0)
    c: Coincident(g2,g-3)
    c: Equal(g1,g2)
    c: DistanceY(g0,g2) = 7
FEATURE [PartDesign::Pocket] Pocket099  label="Pocket099-vertical_inset"
  BaseFeature = -> Pocket098
  Direction = (1,0,0)
  Length = 3
  Length2 = 5
  Profile = -> Sketch213
  ReferenceAxis = -> Sketch213 [N_Axis]
  Type = 0
FEATURE [Sketcher::SketchObject] Sketch214
  ExternalGeometry = -> [Pocket099]
  FullyConstrained = true
  MapMode = 5
  Placement = pos=(0,0,3) rot=(0,0,1;0rad)
  Support = -> [Pocket099]
  sketch-geometry (2):
    g0: Circle CenterX=10 CenterY=-6 CenterZ=0 NormalX=0 NormalY=0 NormalZ=1 AngleXU=0 Radius=2.65
    g1: Circle CenterX=10 CenterY=-34 CenterZ=0 NormalX=0 NormalY=0 NormalZ=1 AngleXU=0 Radius=2.65
  constraints (4):
    c: Coincident(g0,g-3)
    c: Coincident(g1,g-4)
    c: Equal(g1,g0)
    c: Diameter(g1) = 5.3
FEATURE [PartDesign::Pocket] Pocket100
  BaseFeature = -> Pocket099
  Direction = (0,0,-1)
  Length = 5
  Length2 = 5
  Profile = -> Sketch214
  ReferenceAxis = -> Sketch214 [N_Axis]
  Type = 0
FEATURE [Sketcher::SketchObject] Sketch215
  ExternalGeometry = -> [Pocket100]
  FullyConstrained = true
  MapMode = 5
  Placement = pos=(3,0,0) rot=(0.57735,-0.57735,-0.57735;2.0944rad)
  Support = -> [Pocket100]
  sketch-geometry (1):
    g0: Circle CenterX=20 CenterY=19 CenterZ=0 NormalX=0 NormalY=0 NormalZ=1 AngleXU=0 Radius=2.65
  constraints (2):
    c: Coincident(g0,g-3)
    c: Diameter(g0) = 5.3
FEATURE [PartDesign::Pocket] Pocket101
  BaseFeature = -> Pocket100
  Direction = (1,0,0)
  Length = 5
  Length2 = 5
  Profile = -> Sketch215
  ReferenceAxis = -> Sketch215 [N_Axis]
  Type = 0
FEATURE [PartDesign::Fillet] Fillet105
  Base = -> Pocket101 [Edge19,Edge21,Edge3]
  BaseFeature = -> Pocket101
  Radius = 2
  SupportTransform = false
  UseAllEdges = false
FEATURE [PartDesign::Chamfer] Chamfer012
  Angle = 45
  Base = -> Fillet105 [Edge54]
  BaseFeature = -> Fillet105
  ChamferType = 0
  FlipDirection = false
  Size = 2.5
  Size2 = 1
  SupportTransform = false
  UseAllEdges = false
FEATURE [PartDesign::Fillet] Fillet106
  Base = -> Chamfer012 [Face31,Face32,Face37]
  BaseFeature = -> Chamfer012
  Radius = 0.5
  SupportTransform = false
  UseAllEdges = false
FEATURE [PartDesign::Fillet] Fillet107
  Base = -> Fillet106 [Face26,Face38]
  BaseFeature = -> Fillet106
  Radius = 0.5
  SupportTransform = false
  UseAllEdges = false
FEATURE [Sketcher::SketchObject] Sketch222
  ExternalGeometry = -> [Fillet107]
  FullyConstrained = true
  MapMode = 5
  Placement = pos=(0,0,0) rot=(0.57735,-0.57735,-0.57735;2.0944rad)
  Support = -> [Fillet107]
  sketch-geometry (5):
    g0: LineSegment StartX=10 StartY=26 StartZ=0 EndX=30 EndY=26 EndZ=0
    g1: LineSegment StartX=30 StartY=26 StartZ=0 EndX=30 EndY=6 EndZ=0
    g2: LineSegment StartX=30 StartY=6 StartZ=0 EndX=10 EndY=6 EndZ=0
    g3: LineSegment StartX=10 StartY=6 StartZ=0 EndX=10 EndY=26 EndZ=0
    g4: GeomPoint X=20 Y=6 Z=0
  constraints (12):
    c: Coincident(g0,g1)
    c: Coincident(g1,g2)
    c: Coincident(g2,g3)
    c: Coincident(g3,g0)
    c: Horizontal(g0)
    c: Horizontal(g2)
    c: Vertical(g1)
    c: Vertical(g3)
    c: DistanceX(g0,g0) = 20
    c: Symmetric(g2,g2,g4)
    c: Symmetric(g-3,g-3,g4)
    c: DistanceY(g1,g1) = 20
FEATURE [PartDesign::Pocket] Pocket106
  BaseFeature = -> Fillet107
  Direction = (1,0,0)
  Length = 2
  Length2 = 5
  Profile = -> Sketch222
  ReferenceAxis = -> Sketch222 [N_Axis]
  Type = 0
FEATURE [PartDesign::Fillet] Fillet116
  Base = -> Pocket106 [Edge73]
  BaseFeature = -> Pocket106
  Radius = 1
  SupportTransform = false
  UseAllEdges = false
FEATURE [PartDesign::Fillet] Fillet117
  Base = -> Fillet116 [Edge34]
  BaseFeature = -> Fillet116
  Radius = 0.5
  SupportTransform = false
  UseAllEdges = false
FEATURE [PartDesign::Fillet] Fillet118
  Base = -> Fillet117 [Face35]
  BaseFeature = -> Fillet117
  Radius = 0.4
  SupportTransform = false
  UseAllEdges = false
FEATURE [PartDesign::Fillet] Fillet119
  Base = -> Fillet118 [Face9]
  BaseFeature = -> Fillet118
  Radius = 1
  SupportTransform = false
  UseAllEdges = false
FEATURE [PartDesign::Body] Body026005
  Group = -> [Sketch210,Pad106,Sketch211,Pad107,Fillet103,Fillet104,Sketch212,Pocket098,Sketch213,Pocket099,Sketch214,Pocket100,Sketch215,Pocket101,Fillet105,Chamfer012,Fillet106,Fillet107,Sketch222,Pocket106,Fillet116,Fillet117,Fillet118,Fillet119]
  Origin = -> Origin039
  Tip = -> Fillet119
COMPONENT P29 — recipe-attached ("Body026005002", modeled in this document).
Construction recipe (the document's own serialized feature program — sketch geometry with constraints, then the solid features built on it; lengths are millimeters unless a unit is written):

FEATURE [Sketcher::SketchObject] Sketch242
  FullyConstrained = true
  MapMode = 5
  Placement = pos=(0,0,0) rot=(0.57735,0.57735,0.57735;2.0944rad)
  Support = -> [YZ_Plane042]
  sketch-geometry (4):
    g0: LineSegment StartX=0 StartY=0 StartZ=0 EndX=30 EndY=0 EndZ=0
    g1: LineSegment StartX=30 StartY=0 StartZ=0 EndX=30 EndY=20 EndZ=0
    g2: LineSegment StartX=30 StartY=20 StartZ=0 EndX=0 EndY=20 EndZ=0
    g3: LineSegment StartX=0 StartY=20 StartZ=0 EndX=0 EndY=0 EndZ=0
  constraints (11):
    c: Coincident(g0,g1)
    c: Coincident(g1,g2)
    c: Coincident(g2,g3)
    c: Coincident(g3,g0)
    c: Horizontal(g0)
    c: Horizontal(g2)
    c: Vertical(g1)
    c: Vertical(g3)
    c: Coincident(g0,g-1)
    c: DistanceX(g0,g0) = 30
    c: DistanceY(g1,g1) = 20
FEATURE [PartDesign::Pad] Pad123  label="Pad123-body"
  Direction = (1,-2e-16,3e-16)
  Length = 8
  Length2 = 10
  Placement = pos=(0,0,0) rot=(0.57735,0.57735,0.57735;2.0944rad)
  Profile = -> Sketch242
  ReferenceAxis = -> Sketch242 [N_Axis]
  Type = 0
FEATURE [Sketcher::SketchObject] Sketch243
  ExternalGeometry = -> [Pad123]
  FullyConstrained = true
  MapMode = 5
  Placement = pos=(-7.8e-15,1.11e-14,20) rot=(0,0,-1;1.5708rad)
  Support = -> [Pad123]
  sketch-geometry (4):
    g0: LineSegment StartX=-12 StartY=8 StartZ=0 EndX=7.1e-15 EndY=8 EndZ=0
    g1: LineSegment StartX=7.1e-15 StartY=8 StartZ=0 EndX=7.1e-15 EndY=3 EndZ=0
    g2: LineSegment StartX=7.1e-15 StartY=3 StartZ=0 EndX=-12 EndY=3 EndZ=0
    g3: LineSegment StartX=-12 StartY=3 StartZ=0 EndX=-12 EndY=8 EndZ=0
  constraints (11):
    c: Coincident(g0,g1)
    c: Coincident(g1,g2)
    c: Coincident(g2,g3)
    c: Coincident(g3,g0)
    c: Horizontal(g0)
    c: Horizontal(g2)
    c: Vertical(g1)
    c: Vertical(g3)
    c: DistanceY(g1,g1) = 5
    c: DistanceX(g2,g2) = 12
    c: Coincident(g0,g-3)
FEATURE [PartDesign::Pad] Pad124  label="Pad124-vertical"
  BaseFeature = -> Pad123
  Direction = (-4e-16,6e-16,1)
  Length = 25
  Length2 = 10
  Placement = pos=(0,0,0) rot=(0.57735,0.57735,0.57735;2.0944rad)
  Profile = -> Sketch243
  ReferenceAxis = -> Sketch243 [N_Axis]
  Type = 0
FEATURE [PartDesign::Fillet] Fillet132  label="Fillet132-vertical"
  Base = -> Pad124 [Edge19,Edge24]
  BaseFeature = -> Pad124
  Placement = pos=(0,0,0) rot=(0.57735,0.57735,0.57735;2.0944rad)
  Radius = 5.95
  SupportTransform = false
  UseAllEdges = false
FEATURE [PartDesign::Fillet] Fillet133  label="Fillet133-vertical_base_short"
  Base = -> Fillet132 [Edge16]
  BaseFeature = -> Fillet132
  Placement = pos=(0,0,0) rot=(0.57735,0.57735,0.57735;2.0944rad)
  Radius = 2
  SupportTransform = false
  UseAllEdges = false
FEATURE [PartDesign::Fillet] Fillet134  label="Fillet134-vertical_base_long"
  Base = -> Fillet133 [Edge26]
  BaseFeature = -> Fillet133
  Placement = pos=(0,0,0) rot=(0.57735,0.57735,0.57735;2.0944rad)
  Radius = 5
  SupportTransform = false
  UseAllEdges = false
FEATURE [PartDesign::Fillet] Fillet135  label="Fillet135-base_corners"
  Base = -> Fillet134 [Edge30,Edge40,Edge34]
  BaseFeature = -> Fillet134
  Placement = pos=(0,0,0) rot=(0.57735,0.57735,0.57735;2.0944rad)
  Radius = 8
  SupportTransform = false
  UseAllEdges = false
FEATURE [Sketcher::SketchObject] Sketch244
  ExternalGeometry = -> [Fillet135]
  FullyConstrained = true
  MapMode = 5
  Placement = pos=(8,-5.3e-15,3.6e-15) rot=(0.57735,0.57735,0.57735;2.0944rad)
  Support = -> [Fillet135]
  sketch-geometry (4):
    g0: ArcOfCircle CenterX=8 CenterY=10 CenterZ=0 NormalX=0 NormalY=0 NormalZ=1 AngleXU=0 Radius=6 StartAngle=1.5708 EndAngle=4.71239
    g1: ArcOfCircle CenterX=22 CenterY=10 CenterZ=0 NormalX=0 NormalY=0 NormalZ=1 AngleXU=0 Radius=6 StartAngle=4.71239 EndAngle=7.85398
    g2: LineSegment StartX=8 StartY=4 StartZ=0 EndX=22 EndY=4 EndZ=0
    g3: LineSegment StartX=22 StartY=16 StartZ=0 EndX=8 EndY=16 EndZ=0
  constraints (10):
    c: Tangent(g0,g2) = -1.5708
    c: Tangent(g2,g1) = -1.5708
    c: Tangent(g1,g3) = -1.5708
    c: Tangent(g3,g0) = -1.5708
    c: Equal(g0,g1)
    c: Horizontal(g1,g0)
    c: Diameter(g0) = 12
    c: DistanceX(g0) = 8
    c: DistanceY(g0) = 10
    c: DistanceX(g1,g-3) = 8
FEATURE [PartDesign::Pocket] Pocket113  label="Pocket113_screw_inset"
  BaseFeature = -> Fillet135
  Direction = (-1,9e-16,-6e-16)
  Length = 2
  Length2 = 5
  Placement = pos=(0,0,0) rot=(0.57735,0.57735,0.57735;2.0944rad)
  Profile = -> Sketch244
  ReferenceAxis = -> Sketch244 [N_Axis]
  Type = 0
FEATURE [Sketcher::SketchObject] Sketch245
  ExternalGeometry = -> [Pocket113]
  FullyConstrained = true
  MapMode = 5
  Placement = pos=(6,-5.3e-15,3.7e-15) rot=(0.57735,0.57735,0.57735;2.0944rad)
  Support = -> [Pocket113]
  sketch-geometry (2):
    g0: Circle CenterX=8 CenterY=10 CenterZ=0 NormalX=0 NormalY=0 NormalZ=1 AngleXU=0 Radius=2.65
    g1: Circle CenterX=22 CenterY=10 CenterZ=0 NormalX=0 NormalY=0 NormalZ=1 AngleXU=0 Radius=2.65
  constraints (4):
    c: Coincident(g0,g-3)
    c: Coincident(g1,g-4)
    c: Equal(g0,g1)
    c: Diameter(g1) = 5.3
FEATURE [PartDesign::Pocket] Pocket114  label="Pocket114-screw_holes"
  BaseFeature = -> Pocket113
  Direction = (-1,8e-16,-6e-16)
  Length = 5
  Length2 = 5
  Placement = pos=(0,0,0) rot=(0.57735,0.57735,0.57735;2.0944rad)
  Profile = -> Sketch245
  ReferenceAxis = -> Sketch245 [N_Axis]
  Type = 1
FEATURE [PartDesign::Chamfer] Chamfer017
  Angle = 45
  Base = -> Pocket114 [Edge9]
  BaseFeature = -> Pocket114
  ChamferType = 0
  FlipDirection = false
  Placement = pos=(0,0,0) rot=(0.57735,0.57735,0.57735;2.0944rad)
  Size = 0.9
  Size2 = 1
  SupportTransform = false
  UseAllEdges = false
FEATURE [PartDesign::Fillet] Fillet136
  Base = -> Chamfer017 [Face4]
  BaseFeature = -> Chamfer017
  Placement = pos=(0,0,0) rot=(0.57735,0.57735,0.57735;2.0944rad)
  Radius = 0.6
  SupportTransform = false
  UseAllEdges = false
FEATURE [PartDesign::Fillet] Fillet137
  Base = -> Fillet136 [Face37,Face36,Face51]
  BaseFeature = -> Fillet136
  Placement = pos=(0,0,0) rot=(0.57735,0.57735,0.57735;2.0944rad)
  Radius = 0.3
  SupportTransform = false
  UseAllEdges = false
FEATURE [PartDesign::Fillet] Fillet138
  Base = -> Fillet137 [Edge58]
  BaseFeature = -> Fillet137
  Placement = pos=(0,0,0) rot=(0.57735,0.57735,0.57735;2.0944rad)
  Radius = 0.6
  SupportTransform = false
  UseAllEdges = false
FEATURE [Sketcher::SketchObject] Sketch246
  ExternalGeometry = -> [Fillet138]
  FullyConstrained = true
  MapMode = 5
  Placement = pos=(8,-5.3e-15,7.5e-15) rot=(0.57735,0.57735,0.57735;2.0944rad)
  Support = -> [Fillet138]
  sketch-geometry (4):
    g0: ArcOfCircle CenterX=5.95 CenterY=39.05 CenterZ=0 NormalX=0 NormalY=0 NormalZ=1 AngleXU=0 Radius=2.5 StartAngle=-9e-16 EndAngle=3.14159
    g1: ArcOfCircle CenterX=5.95 CenterY=25.05 CenterZ=0 NormalX=0 NormalY=0 NormalZ=1 AngleXU=0 Radius=2.5 StartAngle=3.14159 EndAngle=6.28319
    g2: LineSegment StartX=3.45 StartY=39.05 StartZ=0 EndX=3.45 EndY=25.05 EndZ=0
    g3: LineSegment StartX=8.45 StartY=25.05 StartZ=0 EndX=8.45 EndY=39.05 EndZ=0
  constraints (9):
    c: Tangent(g0,g2) = -1.5708
    c: Tangent(g2,g1) = -1.5708
    c: Tangent(g1,g3) = -1.5708
    c: Tangent(g3,g0) = -1.5708
    c: Equal(g0,g1)
    c: Coincident(g0,g-3)
    c: Vertical(g2)
    c: DistanceY(g1,g0) = 14
    c: Diameter(g0) = 5
FEATURE [PartDesign::Pocket] Pocket115
  BaseFeature = -> Fillet138
  Direction = (-1,7e-16,-1.1e-15)
  Length = 5
  Length2 = 5
  Placement = pos=(0,0,0) rot=(0.57735,0.57735,0.57735;2.0944rad)
  Profile = -> Sketch246
  ReferenceAxis = -> Sketch246 [N_Axis]
  Type = 1
FEATURE [PartDesign::Fillet] Fillet139
  Base = -> Pocket115 [Face61]
  BaseFeature = -> Pocket115
  Placement = pos=(0,0,0) rot=(0.57735,0.57735,0.57735;2.0944rad)
  Radius = 1
  SupportTransform = false
  UseAllEdges = false
FEATURE [PartDesign::Body] Body026005002
  Group = -> [Sketch242,Pad123,Sketch243,Pad124,Fillet132,Fillet133,Fillet134,Fillet135,Sketch244,Pocket113,Sketch245,Pocket114,Chamfer017,Fillet136,Fillet137,Fillet138,Sketch246,Pocket115,Fillet139]
  Origin = -> Origin041
  Tip = -> Fillet139
COMPONENT P30 — recipe-attached ("Body026006", modeled in this document).
Construction recipe (the document's own serialized feature program — sketch geometry with constraints, then the solid features built on it; lengths are millimeters unless a unit is written):

FEATURE [Sketcher::SketchObject] Sketch216
  FullyConstrained = true
  MapMode = 5
  Support = -> [XY_Plane040]
  sketch-geometry (4):
    g0: LineSegment StartX=0 StartY=0 StartZ=0 EndX=20 EndY=0 EndZ=0
    g1: LineSegment StartX=20 StartY=0 StartZ=0 EndX=20 EndY=-40 EndZ=0
    g2: LineSegment StartX=20 StartY=-40 StartZ=0 EndX=0 EndY=-40 EndZ=0
    g3: LineSegment StartX=0 StartY=-40 StartZ=0 EndX=0 EndY=0 EndZ=0
  constraints (11):
    c: Coincident(g0,g1)
    c: Coincident(g1,g2)
    c: Coincident(g2,g3)
    c: Coincident(g3,g0)
    c: Horizontal(g0)
    c: Horizontal(g2)
    c: Vertical(g1)
    c: Vertical(g3)
    c: Coincident(g0,g-1)
    c: DistanceX(g2,g2) = 20
    c: DistanceY(g1,g1) = 40
FEATURE [PartDesign::Pad] Pad108  label="Pad106-base001"
  Direction = (0,0,1)
  Length = 6
  Length2 = 10
  Profile = -> Sketch216
  ReferenceAxis = -> Sketch216 [N_Axis]
  Type = 0
FEATURE [Sketcher::SketchObject] Sketch217
  FullyConstrained = true
  MapMode = 5
  Placement = pos=(0,0,6) rot=(0,0,1;0rad)
  Support = -> [Pad108]
  sketch-geometry (4):
    g0: LineSegment StartX=0 StartY=-14.5 StartZ=0 EndX=20 EndY=-14.5 EndZ=0
    g1: LineSegment StartX=20 StartY=-14.5 StartZ=0 EndX=20 EndY=-20.5 EndZ=0
    g2: LineSegment StartX=20 StartY=-20.5 StartZ=0 EndX=0 EndY=-20.5 EndZ=0
    g3: LineSegment StartX=0 StartY=-20.5 StartZ=0 EndX=0 EndY=-14.5 EndZ=0
  constraints (12):
    c: Coincident(g0,g1)
    c: Coincident(g1,g2)
    c: Coincident(g2,g3)
    c: Coincident(g3,g0)
    c: Horizontal(g0)
    c: Horizontal(g2)
    c: Vertical(g1)
    c: Vertical(g3)
    c: DistanceX(g2,g2) = 20
    c: DistanceY(g3,g3) = 6
    c: PointOnObject(g2,g-2)
    c: DistanceY(g0) = -14.5
FEATURE [PartDesign::Pad] Pad109  label="Pad107-vertical001"
  BaseFeature = -> Pad108
  Direction = (0,0,1)
  Length = 20
  Length2 = 10
  Profile = -> Sketch217
  ReferenceAxis = -> Sketch217 [N_Axis]
  Type = 0
FEATURE [PartDesign::Fillet] Fillet110  label="Fillet103-base001"
  Base = -> Pad109 [Edge5,Edge10,Edge1,Edge2]
  BaseFeature = -> Pad109
  Radius = 9
  SupportTransform = false
  UseAllEdges = false
FEATURE [Sketcher::SketchObject] Sketch218
  ExternalGeometry = -> [Fillet110]
  FullyConstrained = true
  MapMode = 5
  Placement = pos=(0,0,6) rot=(0,0,1;0rad)
  Support = -> [Fillet110]
  sketch-geometry (5):
    g0: Circle CenterX=10 CenterY=-7 CenterZ=0 NormalX=0 NormalY=0 NormalZ=1 AngleXU=0 Radius=5
    g1: Circle CenterX=10 CenterY=-33 CenterZ=0 NormalX=0 NormalY=0 NormalZ=1 AngleXU=0 Radius=5
    g2: LineSegment StartX=9 StartY=0 StartZ=0 EndX=10 EndY=-7 EndZ=0
    g3: LineSegment StartX=10 StartY=-7 StartZ=0 EndX=11 EndY=0 EndZ=0
    g4: LineSegment StartX=10 StartY=-33 StartZ=0 EndX=9 EndY=-40 EndZ=0
  constraints (12):
    c: Equal(g1,g0)
    c: Vertical(g1,g0)
    c: Coincident(g2,g-3)
    c: Coincident(g2,g0)
    c: Coincident(g3,g0)
    c: Coincident(g3,g-3)
    c: Equal(g3,g2)
    c: DistanceY(g0) = -7
    c: Diameter(g0) = 10
    c: Coincident(g4,g1)
    c: Coincident(g4,g-4)
    c: Equal(g4,g2)
FEATURE [PartDesign::Pocket] Pocket102  label="Pocket102-base_inset"
  BaseFeature = -> Fillet110
  Direction = (0,0,-1)
  Length = 3
  Length2 = 5
  Profile = -> Sketch218
  ReferenceAxis = -> Sketch218 [N_Axis]
  Type = 0
FEATURE [Sketcher::SketchObject] Sketch219
  ExternalGeometry = -> [Pocket102]
  FullyConstrained = true
  MapMode = 5
  Placement = pos=(0,0,3) rot=(0,0,1;0rad)
  Support = -> [Pocket102]
  sketch-geometry (2):
    g0: Circle CenterX=10 CenterY=-7 CenterZ=0 NormalX=0 NormalY=0 NormalZ=1 AngleXU=0 Radius=2.65
    g1: Circle CenterX=10 CenterY=-33 CenterZ=0 NormalX=0 NormalY=0 NormalZ=1 AngleXU=0 Radius=2.65
  constraints (4):
    c: Coincident(g0,g-3)
    c: Coincident(g1,g-4)
    c: Equal(g1,g0)
    c: Diameter(g0) = 5.3
FEATURE [PartDesign::Pocket] Pocket103
  BaseFeature = -> Pocket102
  Direction = (0,0,-1)
  Length = 5
  Length2 = 5
  Profile = -> Sketch219
  ReferenceAxis = -> Sketch219 [N_Axis]
  Type = 0
FEATURE [PartDesign::Fillet] Fillet111
  Base = -> Pocket103 [Edge45,Edge47]
  BaseFeature = -> Pocket103
  Radius = 9
  SupportTransform = false
  UseAllEdges = false
FEATURE [Sketcher::SketchObject] Sketch220
  ExternalGeometry = -> [Fillet111]
  FullyConstrained = true
  MapMode = 5
  Placement = pos=(0,-14.5,0) rot=(0,0.707107,0.707107;3.14159rad)
  Support = -> [Fillet111]
  sketch-geometry (3):
    g0: Circle CenterX=-10 CenterY=20 CenterZ=0 NormalX=0 NormalY=0 NormalZ=1 AngleXU=0 Radius=5
    g1: LineSegment StartX=-11 StartY=26 StartZ=0 EndX=-10 EndY=20 EndZ=0
    g2: LineSegment StartX=-10 StartY=20 StartZ=0 EndX=-9 EndY=26 EndZ=0
  constraints (7):
    c: Coincident(g1,g-3)
    c: Coincident(g1,g0)
    c: Coincident(g2,g0)
    c: Coincident(g2,g-3)
    c: Equal(g2,g1)
    c: DistanceY(g0,g2) = 6
    c: Diameter(g0) = 10
FEATURE [PartDesign::Pocket] Pocket104
  BaseFeature = -> Fillet111
  Direction = (0,-1,2e-16)
  Length = 3
  Length2 = 5
  Profile = -> Sketch220
  ReferenceAxis = -> Sketch220 [N_Axis]
  Type = 0
FEATURE [Sketcher::SketchObject] Sketch221
  ExternalGeometry = -> [Pocket104]
  FullyConstrained = true
  MapMode = 5
  Placement = pos=(2.1e-15,-17.5,3.7e-15) rot=(0,0.707107,0.707107;3.14159rad)
  Support = -> [Pocket104]
  sketch-geometry (1):
    g0: Circle CenterX=-10 CenterY=20 CenterZ=0 NormalX=0 NormalY=0 NormalZ=1 AngleXU=0 Radius=2.65
  constraints (2):
    c: Coincident(g0,g-3)
    c: Diameter(g0) = 5.3
FEATURE [PartDesign::Pocket] Pocket105
  BaseFeature = -> Pocket104
  Direction = (1e-16,-1,2e-16)
  Length = 5
  Length2 = 5
  Profile = -> Sketch221
  ReferenceAxis = -> Sketch221 [N_Axis]
  Type = 0
FEATURE [PartDesign::Fillet] Fillet112
  Base = -> Pocket105 [Edge3,Edge27]
  BaseFeature = -> Pocket105
  Radius = 2
  SupportTransform = false
  UseAllEdges = false
FEATURE [PartDesign::Chamfer] Chamfer013
  Angle = 45
  Base = -> Fillet112 [Edge57]
  BaseFeature = -> Fillet112
  ChamferType = 0
  FlipDirection = false
  Size = 2.5
  Size2 = 1
  SupportTransform = false
  UseAllEdges = false
FEATURE [PartDesign::Fillet] Fillet113
  Base = -> Chamfer013 [Face29,Face34,Face28,Face36,Face37,Face31]
  BaseFeature = -> Chamfer013
  Radius = 0.5
  SupportTransform = false
  UseAllEdges = false
FEATURE [PartDesign::Fillet] Fillet114
  Base = -> Fillet113 [Face32]
  BaseFeature = -> Fillet113
  Radius = 0.5
  SupportTransform = false
  UseAllEdges = false
FEATURE [PartDesign::Fillet] Fillet115
  Base = -> Fillet114 [Edge123]
  BaseFeature = -> Fillet114
  Radius = 0.4
  SupportTransform = false
  UseAllEdges = false
FEATURE [PartDesign::Body] Body026006
  Group = -> [Sketch216,Pad108,Sketch217,Pad109,Fillet110,Sketch218,Pocket102,Sketch219,Pocket103,Fillet111,Sketch220,Pocket104,Sketch221,Pocket105,Fillet112,Chamfer013,Fillet113,Fillet114,Fillet115]
  Origin = -> Origin040
  Tip = -> Fillet115
